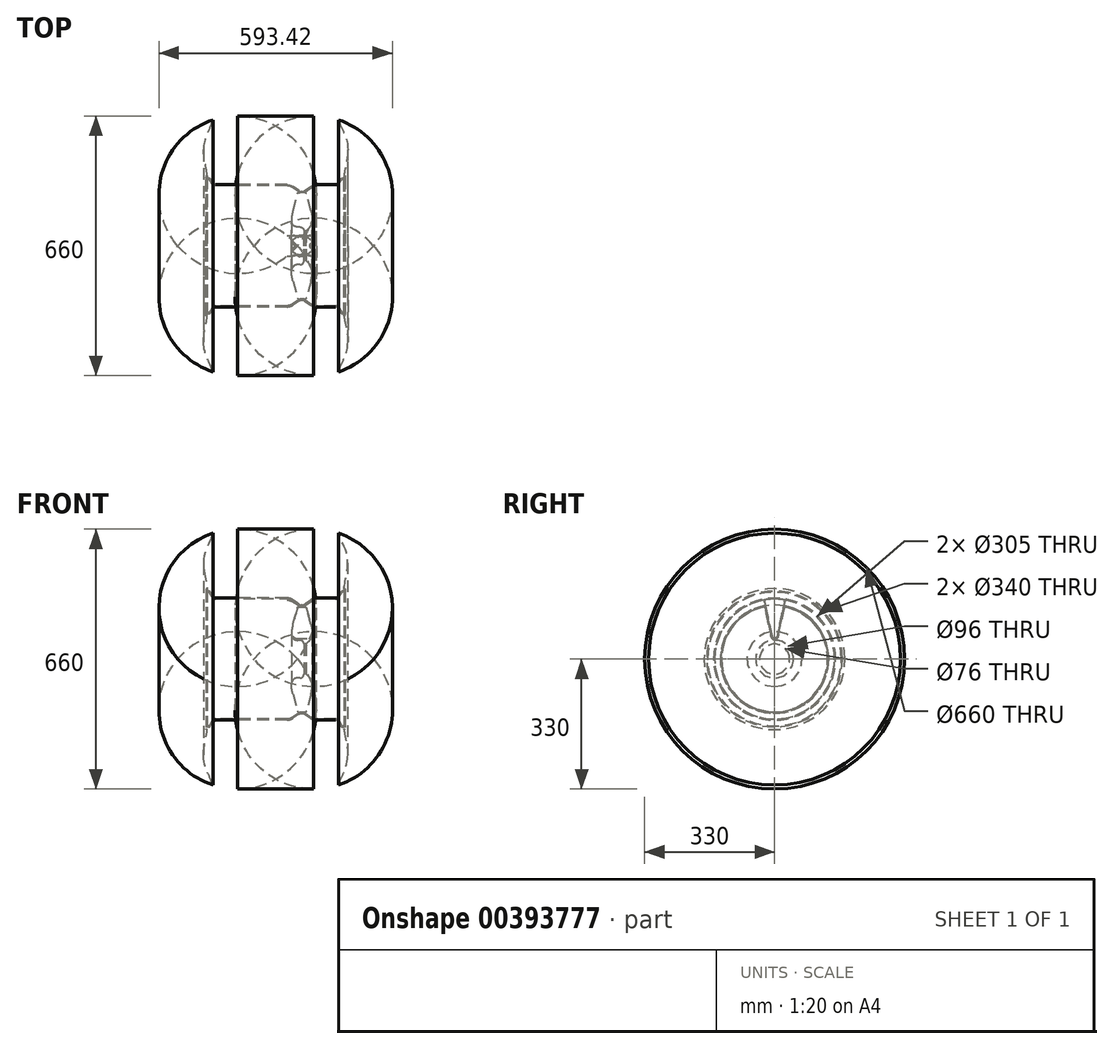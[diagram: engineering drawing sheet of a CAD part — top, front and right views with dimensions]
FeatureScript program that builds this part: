
annotation { "Feature Type Name" : "Feature", "Feature Type Description" : "" }
export const myFeature = defineFeature(function(context is Context, id is Id, definition is map)
    precondition{}
    {
        {
            var Q0;
            Q0=qCreatedBy(makeId("Front.planeOp"),FACE);
            var sketch = newSketch(context, id + "F0", { "sketchPlane" : qUnion([Q0])});
            skLineSegment(sketch, "E0", {"start": v(42.96, 147.98) * mm, "end": v(57.63, 137.71) * mm});
            skLineSegment(sketch, "E1", {"start": v(66.23, 135) * mm, "end": v(66.77, 135) * mm});
            skLineSegment(sketch, "E2", {"start": v(75.37, 137.71) * mm, "end": v(90.04, 147.98) * mm});
            skLineSegment(sketch, "E3", {"start": v(104.38, 152.5) * mm, "end": v(152.7, 152.5) * mm});
            skLineSegment(sketch, "E4", {"start": v(170.82, 170) * mm, "end": v(172.5, 170) * mm});
            skLineSegment(sketch, "E5", {"start": v(176.5, 174) * mm, "end": v(176.5, 178) * mm});
            skLineSegment(sketch, "E6", {"start": v(-170.82, 170) * mm, "end": v(-172.5, 170) * mm});
            skLineSegment(sketch, "E7", {"start": v(-176.5, 174) * mm, "end": v(-176.5, 178) * mm});
            skLineSegment(sketch, "E8", {"start": v(-152.7, 152.5) * mm, "end": v(28.62, 152.5) * mm});
            skLineSegment(sketch, "E9", {"start": v(-167.35, 167.98) * mm, "end": v(-161.38, 157.54) * mm});
            skLineSegment(sketch, "E10", {"start": v(161.38, 157.54) * mm, "end": v(167.35, 167.98) * mm});
            skPoint(sketch, "E11.visualSharp", {"position": v(176.5, 170) * mm});
            skArc(sketch, "E11.filletArc", {"start": v(172.5, 170) * mm, "mid": v(175.33, 171.17) * mm, "end": v(176.5, 174) * mm});
            skPoint(sketch, "E12.visualSharp", {"position": v(-176.5, 170) * mm});
            skArc(sketch, "E12.filletArc", {"start": v(-176.5, 174) * mm, "mid": v(-175.33, 171.17) * mm, "end": v(-172.5, 170) * mm});
            skPoint(sketch, "E13.visualSharp", {"position": v(-158.5, 152.5) * mm});
            skArc(sketch, "E13.filletArc", {"start": v(-161.38, 157.54) * mm, "mid": v(-157.72, 153.85) * mm, "end": v(-152.7, 152.5) * mm});
            skPoint(sketch, "E14.visualSharp", {"position": v(158.5, 152.5) * mm});
            skArc(sketch, "E14.filletArc", {"start": v(152.7, 152.5) * mm, "mid": v(157.72, 153.85) * mm, "end": v(161.38, 157.54) * mm});
            skPoint(sketch, "E15.visualSharp", {"position": v(-168.5, 170) * mm});
            skArc(sketch, "E15.filletArc", {"start": v(-167.35, 167.98) * mm, "mid": v(-168.81, 169.46) * mm, "end": v(-170.82, 170) * mm});
            skPoint(sketch, "E16.visualSharp", {"position": v(168.5, 170) * mm});
            skArc(sketch, "E16.filletArc", {"start": v(170.82, 170) * mm, "mid": v(168.81, 169.46) * mm, "end": v(167.35, 167.98) * mm});
            skPoint(sketch, "E17.visualSharp", {"position": v(36.5, 152.5) * mm});
            skArc(sketch, "E17.filletArc", {"start": v(42.96, 147.98) * mm, "mid": v(36.14, 151.34) * mm, "end": v(28.62, 152.5) * mm});
            skPoint(sketch, "E18.visualSharp", {"position": v(96.5, 152.5) * mm});
            skArc(sketch, "E18.filletArc", {"start": v(104.38, 152.5) * mm, "mid": v(96.86, 151.34) * mm, "end": v(90.04, 147.98) * mm});
            skPoint(sketch, "E19.visualSharp", {"position": v(71.5, 135) * mm});
            skArc(sketch, "E19.filletArc", {"start": v(66.77, 135) * mm, "mid": v(71.28, 135.7) * mm, "end": v(75.37, 137.71) * mm});
            skPoint(sketch, "E20.visualSharp", {"position": v(61.5, 135) * mm});
            skArc(sketch, "E20.filletArc", {"start": v(57.63, 137.71) * mm, "mid": v(61.72, 135.7) * mm, "end": v(66.23, 135) * mm});
            skLineSegment(sketch, "E21.0", {"start": v(174, 174) * mm, "end": v(174, 178) * mm});
            skArc(sketch, "E21.1", {"start": v(172.5, 172.5) * mm, "mid": v(173.56, 172.94) * mm, "end": v(174, 174) * mm});
            skLineSegment(sketch, "E21.2", {"start": v(170.82, 172.5) * mm, "end": v(172.5, 172.5) * mm});
            skArc(sketch, "E21.3", {"start": v(170.82, 172.5) * mm, "mid": v(167.56, 171.62) * mm, "end": v(165.18, 169.22) * mm});
            skLineSegment(sketch, "E21.4", {"start": v(159.2, 158.78) * mm, "end": v(165.18, 169.22) * mm});
            skArc(sketch, "E21.5", {"start": v(152.7, 155) * mm, "mid": v(156.46, 156.01) * mm, "end": v(159.2, 158.78) * mm});
            skLineSegment(sketch, "E21.6", {"start": v(104.38, 155) * mm, "end": v(152.7, 155) * mm});
            skArc(sketch, "E21.7", {"start": v(104.38, 155) * mm, "mid": v(96.11, 153.73) * mm, "end": v(88.61, 150.03) * mm});
            skLineSegment(sketch, "E21.8", {"start": v(73.94, 139.76) * mm, "end": v(88.61, 150.03) * mm});
            skArc(sketch, "E21.9", {"start": v(66.77, 137.5) * mm, "mid": v(70.53, 138.08) * mm, "end": v(73.94, 139.76) * mm});
            skLineSegment(sketch, "E21.10", {"start": v(66.23, 137.5) * mm, "end": v(66.77, 137.5) * mm});
            skArc(sketch, "E21.11", {"start": v(-165.18, 169.22) * mm, "mid": v(-167.56, 171.62) * mm, "end": v(-170.82, 172.5) * mm});
            skLineSegment(sketch, "E21.12", {"start": v(-170.82, 172.5) * mm, "end": v(-172.5, 172.5) * mm});
            skArc(sketch, "E21.13", {"start": v(-174, 174) * mm, "mid": v(-173.56, 172.94) * mm, "end": v(-172.5, 172.5) * mm});
            skLineSegment(sketch, "E21.14", {"start": v(-174, 174) * mm, "end": v(-174, 178) * mm});
            skLineSegment(sketch, "E21.15", {"start": v(-165.18, 169.22) * mm, "end": v(-159.2, 158.78) * mm});
            skArc(sketch, "E21.16", {"start": v(-159.2, 158.78) * mm, "mid": v(-156.46, 156.01) * mm, "end": v(-152.7, 155) * mm});
            skLineSegment(sketch, "E21.17", {"start": v(-152.7, 155) * mm, "end": v(28.62, 155) * mm});
            skArc(sketch, "E21.18", {"start": v(44.39, 150.03) * mm, "mid": v(36.89, 153.73) * mm, "end": v(28.62, 155) * mm});
            skLineSegment(sketch, "E21.19", {"start": v(44.39, 150.03) * mm, "end": v(59.06, 139.76) * mm});
            skArc(sketch, "E21.20", {"start": v(59.06, 139.76) * mm, "mid": v(62.47, 138.08) * mm, "end": v(66.23, 137.5) * mm});
            skLineSegment(sketch, "E22", {"start": v(175.5, 179) * mm, "end": v(175, 179) * mm});
            skLineSegment(sketch, "E23", {"start": v(-175.5, 179) * mm, "end": v(-175, 179) * mm});
            skPoint(sketch, "E24.visualSharp", {"position": v(-176.5, 179) * mm});
            skArc(sketch, "E24.filletArc", {"start": v(-175.5, 179) * mm, "mid": v(-176.2, 178.7) * mm, "end": v(-176.5, 178) * mm});
            skPoint(sketch, "E25.visualSharp", {"position": v(-174, 179) * mm});
            skArc(sketch, "E25.filletArc", {"start": v(-174, 178) * mm, "mid": v(-174.3, 178.7) * mm, "end": v(-175, 179) * mm});
            skPoint(sketch, "E26.visualSharp", {"position": v(174, 179) * mm});
            skArc(sketch, "E26.filletArc", {"start": v(175, 179) * mm, "mid": v(174.3, 178.7) * mm, "end": v(174, 178) * mm});
            skPoint(sketch, "E27.visualSharp", {"position": v(176.5, 179) * mm});
            skArc(sketch, "E27.filletArc", {"start": v(176.5, 178) * mm, "mid": v(176.2, 178.7) * mm, "end": v(175.5, 179) * mm});
            skLineSegment(sketch, "E28", {"start": v(-244.06, 0) * mm, "end": v(333.32, 0) * mm, "construction": true});
            skLineSegment(sketch, "E29", {"start": v(76.33, 138.38) * mm, "end": v(89.6, 88.88) * mm});
            skArc(sketch, "E30", {"start": v(89.6, 88.88) * mm, "mid": v(92.14, 76.05) * mm, "end": v(93, 63) * mm});
            skLineSegment(sketch, "E31", {"start": v(93, 63) * mm, "end": v(93, 94.03) * mm, "construction": true});
            skLineSegment(sketch, "E32", {"start": v(61.79, 48) * mm, "end": v(55.2, 48) * mm});
            skArc(sketch, "E33", {"start": v(55.2, 48) * mm, "mid": v(44.6, 52.4) * mm, "end": v(40.2, 63) * mm});
            skArc(sketch, "E34", {"start": v(40.2, 63) * mm, "mid": v(41.06, 76.05) * mm, "end": v(43.6, 88.88) * mm});
            skLineSegment(sketch, "E35", {"start": v(40.2, 63) * mm, "end": v(40.2, 94.03) * mm, "construction": true});
            skLineSegment(sketch, "E36", {"start": v(43.6, 88.88) * mm, "end": v(56.84, 138.26) * mm});
            skLineSegment(sketch, "E37", {"start": v(71.79, 38) * mm, "end": v(71.79, 38) * mm});
            skLineSegment(sketch, "E38", {"start": v(71.79, 38) * mm, "end": v(76.79, 38) * mm});
            skLineSegment(sketch, "E39", {"start": v(76.79, 38) * mm, "end": v(86.79, 48) * mm});
            skPoint(sketch, "E40.visualSharp", {"position": v(71.79, 48) * mm});
            skArc(sketch, "E40.filletArc", {"start": v(71.79, 38) * mm, "mid": v(68.86, 45.07) * mm, "end": v(61.79, 48) * mm});
            skArc(sketch, "E41", {"start": v(93, 63) * mm, "mid": v(91.39, 54.88) * mm, "end": v(86.79, 48) * mm});
            skFitSpline(sketch, "E42", {"points": [v(174, 178) * mm, v(174.59, 185.53) * mm, v(180.27, 215) * mm, v(181.17, 263.96) * mm, v(164.85, 306.38) * mm, v(162.5, 319.35) * mm], "startDerivative": vector(0, 85.85) * mm, "endDerivative": vector(0, 123.55) * mm});
            skLineSegment(sketch, "E43", {"start": v(162.5, 319.35) * mm, "end": v(162.5, 293.42) * mm, "construction": true});
            skFitSpline(sketch, "E44", {"points": [v(-162.5, 319.35) * mm, v(-164.85, 306.38) * mm, v(-181.17, 263.96) * mm, v(-180.27, 215) * mm, v(-174.59, 185.53) * mm, v(-174, 178) * mm], "startDerivative": vector(0, -123.55) * mm, "endDerivative": vector(0, -85.85) * mm});
            skLineSegment(sketch, "E45", {"start": v(-162.5, 319.35) * mm, "end": v(-162.5, 293.42) * mm, "construction": true});
            skArc(sketch, "E46.filletArc", {"start": v(162.6, 315.55) * mm, "mid": v(161.56, 318.3) * mm, "end": v(159.16, 320) * mm});
            skArc(sketch, "E47.filletArc", {"start": v(-159.16, 320) * mm, "mid": v(-161.56, 318.3) * mm, "end": v(-162.6, 315.55) * mm});
            skPoint(sketch, "E48", {"position": v(162.5, 306.38) * mm});
            skArc(sketch, "E49", {"start": v(-159.16, 320) * mm, "mid": v(-128.33, 327.48) * mm, "end": v(-96.71, 330) * mm});
            skArc(sketch, "E50", {"start": v(159.16, 320) * mm, "mid": v(128.33, 327.48) * mm, "end": v(96.71, 330) * mm});
            skLineSegment(sketch, "E51", {"start": v(-96.71, 330) * mm, "end": v(96.71, 330) * mm});
            skSolve(sketch);
        }
        {
            var Q0;
            Q0=qCreatedBy(makeId("Right.planeOp"),FACE);
            var sketch = newSketch(context, id + "F1", { "sketchPlane" : qUnion([Q0])});
            skArc(sketch, "E52", {"start": v(-29.75, 149.57) * mm, "mid": v(0, 152.5) * mm, "end": v(29.75, 149.57) * mm, "construction": true});
            skLineSegment(sketch, "E53", {"start": v(-29.75, 149.57) * mm, "end": v(0, 0) * mm, "construction": true});
            skLineSegment(sketch, "E54", {"start": v(29.75, 149.57) * mm, "end": v(0, 0) * mm, "construction": true});
            skArc(sketch, "E55", {"start": v(10.34, 51.98) * mm, "mid": v(0, 53) * mm, "end": v(-10.34, 51.98) * mm, "construction": true});
            skLineSegment(sketch, "E56", {"start": v(0, 0) * mm, "end": v(-34.81, 197.43) * mm, "construction": true});
            skLineSegment(sketch, "E57", {"start": v(0, 0) * mm, "end": v(34.81, 197.43) * mm, "construction": true});
            skArc(sketch, "E58", {"start": v(26.48, 150.18) * mm, "mid": v(0, 152.5) * mm, "end": v(-26.48, 150.18) * mm});
            skLineSegment(sketch, "E59", {"start": v(0, 0) * mm, "end": v(19.74, 187.83) * mm, "construction": true});
            skLineSegment(sketch, "E60", {"start": v(0, 0) * mm, "end": v(-19.74, 187.83) * mm, "construction": true});
            skLineSegment(sketch, "E61", {"start": v(-6.78, 58.48) * mm, "end": v(-26.48, 150.18) * mm});
            skLineSegment(sketch, "E62", {"start": v(6.78, 58.48) * mm, "end": v(26.48, 150.18) * mm});
            skPoint(sketch, "E63.visualSharp", {"position": v(-5.54, 52.7) * mm});
            skArc(sketch, "E63.filletArc", {"start": v(-6.78, 58.48) * mm, "mid": v(-4.36, 54.54) * mm, "end": v(0, 53) * mm});
            skPoint(sketch, "E64.visualSharp", {"position": v(5.54, 52.7) * mm});
            skArc(sketch, "E64.filletArc", {"start": v(0, 53) * mm, "mid": v(4.36, 54.54) * mm, "end": v(6.78, 58.48) * mm});
            skSolve(sketch);
        }
        {
            var Q0;
            Q0=makeQuery(id+"F0.imprint","IMPRINT",FACE,{"disambiguationData":[TD([[makeQuery(id+"F0.imprint","IMPRINT",EDGE,{"derivedFrom":sQuery(id+"F0.wireOp",EDGE,"E3")}),1.0]])]});
            var Q1;
            Q1=sQuery(id+"F0.wireOp",EDGE,"E28");
            revolve(context, id + "F2", {"entities" : qUnion([Q0]), "axis" : qUnion([Q1]), "revolveType" : RevolveType.FULL});
        }
        {
            var Q0;
            Q0=makeQuery(id+"F0.imprint","IMPRINT",FACE,{"disambiguationData":[TD([[makeQuery(id+"F0.imprint","IMPRINT",EDGE,{"derivedFrom":sQuery(id+"F0.wireOp",EDGE,"E1")}),-1.0]])]});
            var Q1;
            Q1=sQuery(id+"F0.wireOp",EDGE,"E28");
            revolve(context, id + "F3", {"entities" : qUnion([Q0]), "axis" : qUnion([Q1]), "revolveType" : RevolveType.FULL});
        }
        {
            var Q0;
            Q0=makeQuery(id+"F1.imprint","IMPRINT",FACE,{"disambiguationData":[TD([[makeQuery(id+"F1.imprint","IMPRINT",EDGE,{"derivedFrom":sQuery(id+"F1.wireOp",EDGE,"E58")}),1.0]])]});
            extrude(context, id + "F4", {"entities" : qUnion([Q0]), "operationType" : NewBodyOperationType.REMOVE, "endBound" : BoundingType.THROUGH_ALL, "oppositeDirection" : true, "depth" : 25 * mm, "hasSecondDirection" : true, "secondDirectionBound" : SecondDirectionBoundingType.THROUGH_ALL, "secondDirectionOppositeDirection" : false, "secondDirectionDepth" : 25 * mm});
        }
        {
            var Q0;
            Q0=makeQuery(id+"F4.boolean.opBoolean","INTERSECT",EDGE,{"derivedFrom":[makeQuery(id+"F3.opRevolve","SWEPT_FACE",FACE,{"disambiguationData":[OSD([sQuery(id+"F0.wireOp",EDGE,"E34")])]}),makeQuery(id+"F4.opExtrude","SWEPT_FACE",FACE,{"disambiguationData":[OSD([sQuery(id+"F1.wireOp",EDGE,"E62")])]})]});
            var Q1;
            Q1=makeQuery(id+"F1MoAnU7Y2teXVl_2.1.F4.boolean.opBoolean","INTERSECT",EDGE,{"derivedFrom":[makeQuery(id+"F3.opRevolve","SWEPT_FACE",FACE,{"disambiguationData":[OSD([sQuery(id+"F0.wireOp",EDGE,"E34")])]}),makeQuery(id+"F1MoAnU7Y2teXVl_2.1.F4.opExtrude","SWEPT_FACE",FACE,{"disambiguationData":[OSD([sQuery(id+"F1.wireOp",EDGE,"E62")])]})]});
            var Q2;
            {var subQ0=sQuery(id+"F1.wireOp",EDGE,"E62");Q2=makeQuery(id+"F1MoAnU7Y2teXVl_2.2.F4.boolean.opBoolean","INTERSECT",EDGE,{"derivedFrom":[makeQuery(id+"F1MoAnU7Y2teXVl_2.1.F4.boolean.opBoolean","SPLIT",FACE,{"disambiguationData":[TD([makeQuery(id+"F4.boolean.opBoolean","COPY",FACE,{"derivedFrom":makeQuery(id+"F4.opExtrude","SWEPT_FACE",FACE,{"disambiguationData":[OSD([subQ0])]})})])],"derivedFrom":makeQuery(id+"F3.opRevolve","SWEPT_FACE",FACE,{"disambiguationData":[OSD([sQuery(id+"F0.wireOp",EDGE,"E34")])]})}),makeQuery(id+"F1MoAnU7Y2teXVl_2.2.F4.opExtrude","SWEPT_FACE",FACE,{"disambiguationData":[OSD([subQ0])]})]});}
            var Q3;
            {var subQ0=sQuery(id+"F1.wireOp",EDGE,"E62");var subQ3=makeQuery(id+"F4.boolean.opBoolean","COPY",FACE,{"derivedFrom":makeQuery(id+"F4.opExtrude","SWEPT_FACE",FACE,{"disambiguationData":[OSD([subQ0])]})});Q3=makeQuery(id+"F1MoAnU7Y2teXVl_2.3.F4.boolean.opBoolean","INTERSECT",EDGE,{"derivedFrom":[makeQuery(id+"F1MoAnU7Y2teXVl_2.2.F4.boolean.opBoolean","SPLIT",FACE,{"disambiguationData":[TD([subQ3])],"derivedFrom":makeQuery(id+"F1MoAnU7Y2teXVl_2.1.F4.boolean.opBoolean","SPLIT",FACE,{"disambiguationData":[TD([subQ3])],"derivedFrom":makeQuery(id+"F3.opRevolve","SWEPT_FACE",FACE,{"disambiguationData":[OSD([sQuery(id+"F0.wireOp",EDGE,"E34")])]})})}),makeQuery(id+"F1MoAnU7Y2teXVl_2.3.F4.opExtrude","SWEPT_FACE",FACE,{"disambiguationData":[OSD([subQ0])]})]});}
            var Q4;
            {var subQ0=sQuery(id+"F1.wireOp",EDGE,"E62");var subQ3=makeQuery(id+"F4.boolean.opBoolean","COPY",FACE,{"derivedFrom":makeQuery(id+"F4.opExtrude","SWEPT_FACE",FACE,{"disambiguationData":[OSD([subQ0])]})});Q4=makeQuery(id+"F1MoAnU7Y2teXVl_2.4.F4.boolean.opBoolean","INTERSECT",EDGE,{"derivedFrom":[makeQuery(id+"F1MoAnU7Y2teXVl_2.3.F4.boolean.opBoolean","SPLIT",FACE,{"disambiguationData":[TD([subQ3])],"derivedFrom":makeQuery(id+"F1MoAnU7Y2teXVl_2.2.F4.boolean.opBoolean","SPLIT",FACE,{"disambiguationData":[TD([subQ3])],"derivedFrom":makeQuery(id+"F1MoAnU7Y2teXVl_2.1.F4.boolean.opBoolean","SPLIT",FACE,{"disambiguationData":[TD([subQ3])],"derivedFrom":makeQuery(id+"F3.opRevolve","SWEPT_FACE",FACE,{"disambiguationData":[OSD([sQuery(id+"F0.wireOp",EDGE,"E34")])]})})})}),makeQuery(id+"F1MoAnU7Y2teXVl_2.4.F4.opExtrude","SWEPT_FACE",FACE,{"disambiguationData":[OSD([subQ0])]})]});}
            var Q5;
            {var subQ0=sQuery(id+"F1.wireOp",EDGE,"E62");var subQ3=makeQuery(id+"F4.boolean.opBoolean","COPY",FACE,{"derivedFrom":makeQuery(id+"F4.opExtrude","SWEPT_FACE",FACE,{"disambiguationData":[OSD([subQ0])]})});Q5=makeQuery(id+"F1MoAnU7Y2teXVl_2.5.F4.boolean.opBoolean","INTERSECT",EDGE,{"derivedFrom":[makeQuery(id+"F1MoAnU7Y2teXVl_2.4.F4.boolean.opBoolean","SPLIT",FACE,{"disambiguationData":[TD([subQ3])],"derivedFrom":makeQuery(id+"F1MoAnU7Y2teXVl_2.3.F4.boolean.opBoolean","SPLIT",FACE,{"disambiguationData":[TD([subQ3])],"derivedFrom":makeQuery(id+"F1MoAnU7Y2teXVl_2.2.F4.boolean.opBoolean","SPLIT",FACE,{"disambiguationData":[TD([subQ3])],"derivedFrom":makeQuery(id+"F1MoAnU7Y2teXVl_2.1.F4.boolean.opBoolean","SPLIT",FACE,{"disambiguationData":[TD([subQ3])],"derivedFrom":makeQuery(id+"F3.opRevolve","SWEPT_FACE",FACE,{"disambiguationData":[OSD([sQuery(id+"F0.wireOp",EDGE,"E34")])]})})})})}),makeQuery(id+"F1MoAnU7Y2teXVl_2.5.F4.opExtrude","SWEPT_FACE",FACE,{"disambiguationData":[OSD([subQ0])]})]});}
            var Q6;
            {var subQ0=sQuery(id+"F1.wireOp",EDGE,"E62");var subQ4=makeQuery(id+"F4.boolean.opBoolean","COPY",FACE,{"derivedFrom":makeQuery(id+"F4.opExtrude","SWEPT_FACE",FACE,{"disambiguationData":[OSD([subQ0])]})});Q6=makeQuery(id+"F1MoAnU7Y2teXVl_2.6.F4.boolean.opBoolean","INTERSECT",EDGE,{"derivedFrom":[makeQuery(id+"F1MoAnU7Y2teXVl_2.5.F4.boolean.opBoolean","SPLIT",FACE,{"disambiguationData":[TD([subQ4])],"derivedFrom":makeQuery(id+"F1MoAnU7Y2teXVl_2.4.F4.boolean.opBoolean","SPLIT",FACE,{"disambiguationData":[TD([subQ4])],"derivedFrom":makeQuery(id+"F1MoAnU7Y2teXVl_2.3.F4.boolean.opBoolean","SPLIT",FACE,{"disambiguationData":[TD([subQ4])],"derivedFrom":makeQuery(id+"F1MoAnU7Y2teXVl_2.2.F4.boolean.opBoolean","SPLIT",FACE,{"disambiguationData":[TD([subQ4])],"derivedFrom":makeQuery(id+"F1MoAnU7Y2teXVl_2.1.F4.boolean.opBoolean","SPLIT",FACE,{"disambiguationData":[TD([subQ4])],"derivedFrom":makeQuery(id+"F3.opRevolve","SWEPT_FACE",FACE,{"disambiguationData":[OSD([sQuery(id+"F0.wireOp",EDGE,"E34")])]})})})})})}),makeQuery(id+"F1MoAnU7Y2teXVl_2.6.F4.opExtrude","SWEPT_FACE",FACE,{"disambiguationData":[OSD([subQ0])]})]});}
            var Q7;
            {var subQ0=sQuery(id+"F1.wireOp",EDGE,"E62");var subQ3=makeQuery(id+"F4.boolean.opBoolean","COPY",FACE,{"derivedFrom":makeQuery(id+"F4.opExtrude","SWEPT_FACE",FACE,{"disambiguationData":[OSD([subQ0])]})});Q7=makeQuery(id+"F1MoAnU7Y2teXVl_2.7.F4.boolean.opBoolean","INTERSECT",EDGE,{"derivedFrom":[makeQuery(id+"F1MoAnU7Y2teXVl_2.6.F4.boolean.opBoolean","SPLIT",FACE,{"disambiguationData":[TD([subQ3])],"derivedFrom":makeQuery(id+"F1MoAnU7Y2teXVl_2.5.F4.boolean.opBoolean","SPLIT",FACE,{"disambiguationData":[TD([subQ3])],"derivedFrom":makeQuery(id+"F1MoAnU7Y2teXVl_2.4.F4.boolean.opBoolean","SPLIT",FACE,{"disambiguationData":[TD([subQ3])],"derivedFrom":makeQuery(id+"F1MoAnU7Y2teXVl_2.3.F4.boolean.opBoolean","SPLIT",FACE,{"disambiguationData":[TD([subQ3])],"derivedFrom":makeQuery(id+"F1MoAnU7Y2teXVl_2.2.F4.boolean.opBoolean","SPLIT",FACE,{"disambiguationData":[TD([subQ3])],"derivedFrom":makeQuery(id+"F1MoAnU7Y2teXVl_2.1.F4.boolean.opBoolean","SPLIT",FACE,{"disambiguationData":[TD([subQ3])],"derivedFrom":makeQuery(id+"F3.opRevolve","SWEPT_FACE",FACE,{"disambiguationData":[OSD([sQuery(id+"F0.wireOp",EDGE,"E34")])]})})})})})})}),makeQuery(id+"F1MoAnU7Y2teXVl_2.7.F4.opExtrude","SWEPT_FACE",FACE,{"disambiguationData":[OSD([subQ0])]})]});}
            var Q8;
            {var subQ0=sQuery(id+"F1.wireOp",EDGE,"E62");var subQ3=makeQuery(id+"F4.boolean.opBoolean","COPY",FACE,{"derivedFrom":makeQuery(id+"F4.opExtrude","SWEPT_FACE",FACE,{"disambiguationData":[OSD([subQ0])]})});Q8=makeQuery(id+"F1MoAnU7Y2teXVl_2.8.F4.boolean.opBoolean","INTERSECT",EDGE,{"derivedFrom":[makeQuery(id+"F1MoAnU7Y2teXVl_2.7.F4.boolean.opBoolean","SPLIT",FACE,{"disambiguationData":[TD([subQ3])],"derivedFrom":makeQuery(id+"F1MoAnU7Y2teXVl_2.6.F4.boolean.opBoolean","SPLIT",FACE,{"disambiguationData":[TD([subQ3])],"derivedFrom":makeQuery(id+"F1MoAnU7Y2teXVl_2.5.F4.boolean.opBoolean","SPLIT",FACE,{"disambiguationData":[TD([subQ3])],"derivedFrom":makeQuery(id+"F1MoAnU7Y2teXVl_2.4.F4.boolean.opBoolean","SPLIT",FACE,{"disambiguationData":[TD([subQ3])],"derivedFrom":makeQuery(id+"F1MoAnU7Y2teXVl_2.3.F4.boolean.opBoolean","SPLIT",FACE,{"disambiguationData":[TD([subQ3])],"derivedFrom":makeQuery(id+"F1MoAnU7Y2teXVl_2.2.F4.boolean.opBoolean","SPLIT",FACE,{"disambiguationData":[TD([subQ3])],"derivedFrom":makeQuery(id+"F1MoAnU7Y2teXVl_2.1.F4.boolean.opBoolean","SPLIT",FACE,{"disambiguationData":[TD([subQ3])],"derivedFrom":makeQuery(id+"F3.opRevolve","SWEPT_FACE",FACE,{"disambiguationData":[OSD([sQuery(id+"F0.wireOp",EDGE,"E34")])]})})})})})})})}),makeQuery(id+"F1MoAnU7Y2teXVl_2.8.F4.opExtrude","SWEPT_FACE",FACE,{"disambiguationData":[OSD([subQ0])]})]});}
            var Q9;
            {var subQ0=sQuery(id+"F1.wireOp",EDGE,"E62");var subQ3=makeQuery(id+"F4.boolean.opBoolean","COPY",FACE,{"derivedFrom":makeQuery(id+"F4.opExtrude","SWEPT_FACE",FACE,{"disambiguationData":[OSD([subQ0])]})});Q9=makeQuery(id+"F1MoAnU7Y2teXVl_2.9.F4.boolean.opBoolean","INTERSECT",EDGE,{"derivedFrom":[makeQuery(id+"F1MoAnU7Y2teXVl_2.8.F4.boolean.opBoolean","SPLIT",FACE,{"disambiguationData":[TD([subQ3])],"derivedFrom":makeQuery(id+"F1MoAnU7Y2teXVl_2.7.F4.boolean.opBoolean","SPLIT",FACE,{"disambiguationData":[TD([subQ3])],"derivedFrom":makeQuery(id+"F1MoAnU7Y2teXVl_2.6.F4.boolean.opBoolean","SPLIT",FACE,{"disambiguationData":[TD([subQ3])],"derivedFrom":makeQuery(id+"F1MoAnU7Y2teXVl_2.5.F4.boolean.opBoolean","SPLIT",FACE,{"disambiguationData":[TD([subQ3])],"derivedFrom":makeQuery(id+"F1MoAnU7Y2teXVl_2.4.F4.boolean.opBoolean","SPLIT",FACE,{"disambiguationData":[TD([subQ3])],"derivedFrom":makeQuery(id+"F1MoAnU7Y2teXVl_2.3.F4.boolean.opBoolean","SPLIT",FACE,{"disambiguationData":[TD([subQ3])],"derivedFrom":makeQuery(id+"F1MoAnU7Y2teXVl_2.2.F4.boolean.opBoolean","SPLIT",FACE,{"disambiguationData":[TD([subQ3])],"derivedFrom":makeQuery(id+"F1MoAnU7Y2teXVl_2.1.F4.boolean.opBoolean","SPLIT",FACE,{"disambiguationData":[TD([subQ3])],"derivedFrom":makeQuery(id+"F3.opRevolve","SWEPT_FACE",FACE,{"disambiguationData":[OSD([sQuery(id+"F0.wireOp",EDGE,"E34")])]})})})})})})})})}),makeQuery(id+"F1MoAnU7Y2teXVl_2.9.F4.opExtrude","SWEPT_FACE",FACE,{"disambiguationData":[OSD([subQ0])]})]});}
            var Q10;
            {var subQ0=sQuery(id+"F1.wireOp",EDGE,"E62");var subQ4=makeQuery(id+"F4.boolean.opBoolean","COPY",FACE,{"derivedFrom":makeQuery(id+"F4.opExtrude","SWEPT_FACE",FACE,{"disambiguationData":[OSD([subQ0])]})});Q10=makeQuery(id+"F1MoAnU7Y2teXVl_2.10.F4.boolean.opBoolean","INTERSECT",EDGE,{"derivedFrom":[makeQuery(id+"F1MoAnU7Y2teXVl_2.9.F4.boolean.opBoolean","SPLIT",FACE,{"disambiguationData":[TD([subQ4])],"derivedFrom":makeQuery(id+"F1MoAnU7Y2teXVl_2.8.F4.boolean.opBoolean","SPLIT",FACE,{"disambiguationData":[TD([subQ4])],"derivedFrom":makeQuery(id+"F1MoAnU7Y2teXVl_2.7.F4.boolean.opBoolean","SPLIT",FACE,{"disambiguationData":[TD([subQ4])],"derivedFrom":makeQuery(id+"F1MoAnU7Y2teXVl_2.6.F4.boolean.opBoolean","SPLIT",FACE,{"disambiguationData":[TD([subQ4])],"derivedFrom":makeQuery(id+"F1MoAnU7Y2teXVl_2.5.F4.boolean.opBoolean","SPLIT",FACE,{"disambiguationData":[TD([subQ4])],"derivedFrom":makeQuery(id+"F1MoAnU7Y2teXVl_2.4.F4.boolean.opBoolean","SPLIT",FACE,{"disambiguationData":[TD([subQ4])],"derivedFrom":makeQuery(id+"F1MoAnU7Y2teXVl_2.3.F4.boolean.opBoolean","SPLIT",FACE,{"disambiguationData":[TD([subQ4])],"derivedFrom":makeQuery(id+"F1MoAnU7Y2teXVl_2.2.F4.boolean.opBoolean","SPLIT",FACE,{"disambiguationData":[TD([subQ4])],"derivedFrom":makeQuery(id+"F1MoAnU7Y2teXVl_2.1.F4.boolean.opBoolean","SPLIT",FACE,{"disambiguationData":[TD([subQ4])],"derivedFrom":makeQuery(id+"F3.opRevolve","SWEPT_FACE",FACE,{"disambiguationData":[OSD([sQuery(id+"F0.wireOp",EDGE,"E34")])]})})})})})})})})})}),makeQuery(id+"F1MoAnU7Y2teXVl_2.10.F4.opExtrude","SWEPT_FACE",FACE,{"disambiguationData":[OSD([subQ0])]})]});}
            var Q11;
            {var subQ0=sQuery(id+"F1.wireOp",EDGE,"E62");var subQ3=makeQuery(id+"F4.boolean.opBoolean","COPY",FACE,{"derivedFrom":makeQuery(id+"F4.opExtrude","SWEPT_FACE",FACE,{"disambiguationData":[OSD([subQ0])]})});Q11=makeQuery(id+"F1MoAnU7Y2teXVl_2.11.F4.boolean.opBoolean","INTERSECT",EDGE,{"derivedFrom":[makeQuery(id+"F1MoAnU7Y2teXVl_2.10.F4.boolean.opBoolean","SPLIT",FACE,{"disambiguationData":[TD([subQ3])],"derivedFrom":makeQuery(id+"F1MoAnU7Y2teXVl_2.9.F4.boolean.opBoolean","SPLIT",FACE,{"disambiguationData":[TD([subQ3])],"derivedFrom":makeQuery(id+"F1MoAnU7Y2teXVl_2.8.F4.boolean.opBoolean","SPLIT",FACE,{"disambiguationData":[TD([subQ3])],"derivedFrom":makeQuery(id+"F1MoAnU7Y2teXVl_2.7.F4.boolean.opBoolean","SPLIT",FACE,{"disambiguationData":[TD([subQ3])],"derivedFrom":makeQuery(id+"F1MoAnU7Y2teXVl_2.6.F4.boolean.opBoolean","SPLIT",FACE,{"disambiguationData":[TD([subQ3])],"derivedFrom":makeQuery(id+"F1MoAnU7Y2teXVl_2.5.F4.boolean.opBoolean","SPLIT",FACE,{"disambiguationData":[TD([subQ3])],"derivedFrom":makeQuery(id+"F1MoAnU7Y2teXVl_2.4.F4.boolean.opBoolean","SPLIT",FACE,{"disambiguationData":[TD([subQ3])],"derivedFrom":makeQuery(id+"F1MoAnU7Y2teXVl_2.3.F4.boolean.opBoolean","SPLIT",FACE,{"disambiguationData":[TD([subQ3])],"derivedFrom":makeQuery(id+"F1MoAnU7Y2teXVl_2.2.F4.boolean.opBoolean","SPLIT",FACE,{"disambiguationData":[TD([subQ3])],"derivedFrom":makeQuery(id+"F1MoAnU7Y2teXVl_2.1.F4.boolean.opBoolean","SPLIT",FACE,{"disambiguationData":[TD([subQ3])],"derivedFrom":makeQuery(id+"F3.opRevolve","SWEPT_FACE",FACE,{"disambiguationData":[OSD([sQuery(id+"F0.wireOp",EDGE,"E34")])]})})})})})})})})})})}),makeQuery(id+"F1MoAnU7Y2teXVl_2.11.F4.opExtrude","SWEPT_FACE",FACE,{"disambiguationData":[OSD([subQ0])]})]});}
            var Q12;
            {var subQ0=sQuery(id+"F1.wireOp",EDGE,"E62");var subQ3=makeQuery(id+"F4.boolean.opBoolean","COPY",FACE,{"derivedFrom":makeQuery(id+"F4.opExtrude","SWEPT_FACE",FACE,{"disambiguationData":[OSD([subQ0])]})});Q12=makeQuery(id+"F1MoAnU7Y2teXVl_2.12.F4.boolean.opBoolean","INTERSECT",EDGE,{"derivedFrom":[makeQuery(id+"F1MoAnU7Y2teXVl_2.11.F4.boolean.opBoolean","SPLIT",FACE,{"disambiguationData":[TD([subQ3])],"derivedFrom":makeQuery(id+"F1MoAnU7Y2teXVl_2.10.F4.boolean.opBoolean","SPLIT",FACE,{"disambiguationData":[TD([subQ3])],"derivedFrom":makeQuery(id+"F1MoAnU7Y2teXVl_2.9.F4.boolean.opBoolean","SPLIT",FACE,{"disambiguationData":[TD([subQ3])],"derivedFrom":makeQuery(id+"F1MoAnU7Y2teXVl_2.8.F4.boolean.opBoolean","SPLIT",FACE,{"disambiguationData":[TD([subQ3])],"derivedFrom":makeQuery(id+"F1MoAnU7Y2teXVl_2.7.F4.boolean.opBoolean","SPLIT",FACE,{"disambiguationData":[TD([subQ3])],"derivedFrom":makeQuery(id+"F1MoAnU7Y2teXVl_2.6.F4.boolean.opBoolean","SPLIT",FACE,{"disambiguationData":[TD([subQ3])],"derivedFrom":makeQuery(id+"F1MoAnU7Y2teXVl_2.5.F4.boolean.opBoolean","SPLIT",FACE,{"disambiguationData":[TD([subQ3])],"derivedFrom":makeQuery(id+"F1MoAnU7Y2teXVl_2.4.F4.boolean.opBoolean","SPLIT",FACE,{"disambiguationData":[TD([subQ3])],"derivedFrom":makeQuery(id+"F1MoAnU7Y2teXVl_2.3.F4.boolean.opBoolean","SPLIT",FACE,{"disambiguationData":[TD([subQ3])],"derivedFrom":makeQuery(id+"F1MoAnU7Y2teXVl_2.2.F4.boolean.opBoolean","SPLIT",FACE,{"disambiguationData":[TD([subQ3])],"derivedFrom":makeQuery(id+"F1MoAnU7Y2teXVl_2.1.F4.boolean.opBoolean","SPLIT",FACE,{"disambiguationData":[TD([subQ3])],"derivedFrom":makeQuery(id+"F3.opRevolve","SWEPT_FACE",FACE,{"disambiguationData":[OSD([sQuery(id+"F0.wireOp",EDGE,"E34")])]})})})})})})})})})})})}),makeQuery(id+"F1MoAnU7Y2teXVl_2.12.F4.opExtrude","SWEPT_FACE",FACE,{"disambiguationData":[OSD([subQ0])]})]});}
            var Q13;
            {var subQ0=sQuery(id+"F1.wireOp",EDGE,"E62");var subQ3=makeQuery(id+"F4.boolean.opBoolean","COPY",FACE,{"derivedFrom":makeQuery(id+"F4.opExtrude","SWEPT_FACE",FACE,{"disambiguationData":[OSD([subQ0])]})});Q13=makeQuery(id+"F1MoAnU7Y2teXVl_2.13.F4.boolean.opBoolean","INTERSECT",EDGE,{"derivedFrom":[makeQuery(id+"F1MoAnU7Y2teXVl_2.12.F4.boolean.opBoolean","SPLIT",FACE,{"disambiguationData":[TD([subQ3])],"derivedFrom":makeQuery(id+"F1MoAnU7Y2teXVl_2.11.F4.boolean.opBoolean","SPLIT",FACE,{"disambiguationData":[TD([subQ3])],"derivedFrom":makeQuery(id+"F1MoAnU7Y2teXVl_2.10.F4.boolean.opBoolean","SPLIT",FACE,{"disambiguationData":[TD([subQ3])],"derivedFrom":makeQuery(id+"F1MoAnU7Y2teXVl_2.9.F4.boolean.opBoolean","SPLIT",FACE,{"disambiguationData":[TD([subQ3])],"derivedFrom":makeQuery(id+"F1MoAnU7Y2teXVl_2.8.F4.boolean.opBoolean","SPLIT",FACE,{"disambiguationData":[TD([subQ3])],"derivedFrom":makeQuery(id+"F1MoAnU7Y2teXVl_2.7.F4.boolean.opBoolean","SPLIT",FACE,{"disambiguationData":[TD([subQ3])],"derivedFrom":makeQuery(id+"F1MoAnU7Y2teXVl_2.6.F4.boolean.opBoolean","SPLIT",FACE,{"disambiguationData":[TD([subQ3])],"derivedFrom":makeQuery(id+"F1MoAnU7Y2teXVl_2.5.F4.boolean.opBoolean","SPLIT",FACE,{"disambiguationData":[TD([subQ3])],"derivedFrom":makeQuery(id+"F1MoAnU7Y2teXVl_2.4.F4.boolean.opBoolean","SPLIT",FACE,{"disambiguationData":[TD([subQ3])],"derivedFrom":makeQuery(id+"F1MoAnU7Y2teXVl_2.3.F4.boolean.opBoolean","SPLIT",FACE,{"disambiguationData":[TD([subQ3])],"derivedFrom":makeQuery(id+"F1MoAnU7Y2teXVl_2.2.F4.boolean.opBoolean","SPLIT",FACE,{"disambiguationData":[TD([subQ3])],"derivedFrom":makeQuery(id+"F1MoAnU7Y2teXVl_2.1.F4.boolean.opBoolean","SPLIT",FACE,{"disambiguationData":[TD([subQ3])],"derivedFrom":makeQuery(id+"F3.opRevolve","SWEPT_FACE",FACE,{"disambiguationData":[OSD([sQuery(id+"F0.wireOp",EDGE,"E34")])]})})})})})})})})})})})})}),makeQuery(id+"F1MoAnU7Y2teXVl_2.13.F4.opExtrude","SWEPT_FACE",FACE,{"disambiguationData":[OSD([subQ0])]})]});}
            var Q14;
            {var subQ0=sQuery(id+"F1.wireOp",EDGE,"E62");var subQ4=makeQuery(id+"F4.boolean.opBoolean","COPY",FACE,{"derivedFrom":makeQuery(id+"F4.opExtrude","SWEPT_FACE",FACE,{"disambiguationData":[OSD([subQ0])]})});Q14=makeQuery(id+"F1MoAnU7Y2teXVl_2.14.F4.boolean.opBoolean","INTERSECT",EDGE,{"derivedFrom":[makeQuery(id+"F1MoAnU7Y2teXVl_2.13.F4.boolean.opBoolean","SPLIT",FACE,{"disambiguationData":[TD([subQ4])],"derivedFrom":makeQuery(id+"F1MoAnU7Y2teXVl_2.12.F4.boolean.opBoolean","SPLIT",FACE,{"disambiguationData":[TD([subQ4])],"derivedFrom":makeQuery(id+"F1MoAnU7Y2teXVl_2.11.F4.boolean.opBoolean","SPLIT",FACE,{"disambiguationData":[TD([subQ4])],"derivedFrom":makeQuery(id+"F1MoAnU7Y2teXVl_2.10.F4.boolean.opBoolean","SPLIT",FACE,{"disambiguationData":[TD([subQ4])],"derivedFrom":makeQuery(id+"F1MoAnU7Y2teXVl_2.9.F4.boolean.opBoolean","SPLIT",FACE,{"disambiguationData":[TD([subQ4])],"derivedFrom":makeQuery(id+"F1MoAnU7Y2teXVl_2.8.F4.boolean.opBoolean","SPLIT",FACE,{"disambiguationData":[TD([subQ4])],"derivedFrom":makeQuery(id+"F1MoAnU7Y2teXVl_2.7.F4.boolean.opBoolean","SPLIT",FACE,{"disambiguationData":[TD([subQ4])],"derivedFrom":makeQuery(id+"F1MoAnU7Y2teXVl_2.6.F4.boolean.opBoolean","SPLIT",FACE,{"disambiguationData":[TD([subQ4])],"derivedFrom":makeQuery(id+"F1MoAnU7Y2teXVl_2.5.F4.boolean.opBoolean","SPLIT",FACE,{"disambiguationData":[TD([subQ4])],"derivedFrom":makeQuery(id+"F1MoAnU7Y2teXVl_2.4.F4.boolean.opBoolean","SPLIT",FACE,{"disambiguationData":[TD([subQ4])],"derivedFrom":makeQuery(id+"F1MoAnU7Y2teXVl_2.3.F4.boolean.opBoolean","SPLIT",FACE,{"disambiguationData":[TD([subQ4])],"derivedFrom":makeQuery(id+"F1MoAnU7Y2teXVl_2.2.F4.boolean.opBoolean","SPLIT",FACE,{"disambiguationData":[TD([subQ4])],"derivedFrom":makeQuery(id+"F1MoAnU7Y2teXVl_2.1.F4.boolean.opBoolean","SPLIT",FACE,{"disambiguationData":[TD([subQ4])],"derivedFrom":makeQuery(id+"F3.opRevolve","SWEPT_FACE",FACE,{"disambiguationData":[OSD([sQuery(id+"F0.wireOp",EDGE,"E34")])]})})})})})})})})})})})})})}),makeQuery(id+"F1MoAnU7Y2teXVl_2.14.F4.opExtrude","SWEPT_FACE",FACE,{"disambiguationData":[OSD([subQ0])]})]});}
            var Q15;
            {var subQ0=sQuery(id+"F1.wireOp",EDGE,"E62");var subQ3=makeQuery(id+"F4.boolean.opBoolean","COPY",FACE,{"derivedFrom":makeQuery(id+"F4.opExtrude","SWEPT_FACE",FACE,{"disambiguationData":[OSD([subQ0])]})});Q15=makeQuery(id+"F1MoAnU7Y2teXVl_2.15.F4.boolean.opBoolean","INTERSECT",EDGE,{"derivedFrom":[makeQuery(id+"F1MoAnU7Y2teXVl_2.14.F4.boolean.opBoolean","SPLIT",FACE,{"disambiguationData":[TD([subQ3])],"derivedFrom":makeQuery(id+"F1MoAnU7Y2teXVl_2.13.F4.boolean.opBoolean","SPLIT",FACE,{"disambiguationData":[TD([subQ3])],"derivedFrom":makeQuery(id+"F1MoAnU7Y2teXVl_2.12.F4.boolean.opBoolean","SPLIT",FACE,{"disambiguationData":[TD([subQ3])],"derivedFrom":makeQuery(id+"F1MoAnU7Y2teXVl_2.11.F4.boolean.opBoolean","SPLIT",FACE,{"disambiguationData":[TD([subQ3])],"derivedFrom":makeQuery(id+"F1MoAnU7Y2teXVl_2.10.F4.boolean.opBoolean","SPLIT",FACE,{"disambiguationData":[TD([subQ3])],"derivedFrom":makeQuery(id+"F1MoAnU7Y2teXVl_2.9.F4.boolean.opBoolean","SPLIT",FACE,{"disambiguationData":[TD([subQ3])],"derivedFrom":makeQuery(id+"F1MoAnU7Y2teXVl_2.8.F4.boolean.opBoolean","SPLIT",FACE,{"disambiguationData":[TD([subQ3])],"derivedFrom":makeQuery(id+"F1MoAnU7Y2teXVl_2.7.F4.boolean.opBoolean","SPLIT",FACE,{"disambiguationData":[TD([subQ3])],"derivedFrom":makeQuery(id+"F1MoAnU7Y2teXVl_2.6.F4.boolean.opBoolean","SPLIT",FACE,{"disambiguationData":[TD([subQ3])],"derivedFrom":makeQuery(id+"F1MoAnU7Y2teXVl_2.5.F4.boolean.opBoolean","SPLIT",FACE,{"disambiguationData":[TD([subQ3])],"derivedFrom":makeQuery(id+"F1MoAnU7Y2teXVl_2.4.F4.boolean.opBoolean","SPLIT",FACE,{"disambiguationData":[TD([subQ3])],"derivedFrom":makeQuery(id+"F1MoAnU7Y2teXVl_2.3.F4.boolean.opBoolean","SPLIT",FACE,{"disambiguationData":[TD([subQ3])],"derivedFrom":makeQuery(id+"F1MoAnU7Y2teXVl_2.2.F4.boolean.opBoolean","SPLIT",FACE,{"disambiguationData":[TD([subQ3])],"derivedFrom":makeQuery(id+"F1MoAnU7Y2teXVl_2.1.F4.boolean.opBoolean","SPLIT",FACE,{"disambiguationData":[TD([subQ3])],"derivedFrom":makeQuery(id+"F3.opRevolve","SWEPT_FACE",FACE,{"disambiguationData":[OSD([sQuery(id+"F0.wireOp",EDGE,"E34")])]})})})})})})})})})})})})})})}),makeQuery(id+"F1MoAnU7Y2teXVl_2.15.F4.opExtrude","SWEPT_FACE",FACE,{"disambiguationData":[OSD([subQ0])]})]});}
            var Q16;
            {var subQ0=sQuery(id+"F1.wireOp",EDGE,"E61");Q16=makeQuery(id+"F1MoAnU7Y2teXVl_2.2.F4.boolean.opBoolean","INTERSECT",EDGE,{"derivedFrom":[makeQuery(id+"F1MoAnU7Y2teXVl_2.1.F4.boolean.opBoolean","SPLIT",FACE,{"disambiguationData":[TD([makeQuery(id+"F4.boolean.opBoolean","COPY",FACE,{"derivedFrom":makeQuery(id+"F4.opExtrude","SWEPT_FACE",FACE,{"disambiguationData":[OSD([sQuery(id+"F1.wireOp",EDGE,"E62")])]})})])],"derivedFrom":makeQuery(id+"F3.opRevolve","SWEPT_FACE",FACE,{"disambiguationData":[OSD([sQuery(id+"F0.wireOp",EDGE,"E30")])]})}),makeQuery(id+"F1MoAnU7Y2teXVl_2.2.F4.opExtrude","SWEPT_FACE",FACE,{"disambiguationData":[OSD([subQ0])]})]});}
            var Q17;
            Q17=makeQuery(id+"F1MoAnU7Y2teXVl_2.1.F4.boolean.opBoolean","INTERSECT",EDGE,{"derivedFrom":[makeQuery(id+"F3.opRevolve","SWEPT_FACE",FACE,{"disambiguationData":[OSD([sQuery(id+"F0.wireOp",EDGE,"E30")])]}),makeQuery(id+"F1MoAnU7Y2teXVl_2.1.F4.opExtrude","SWEPT_FACE",FACE,{"disambiguationData":[OSD([sQuery(id+"F1.wireOp",EDGE,"E61")])]})]});
            var Q18;
            Q18=makeQuery(id+"F4.boolean.opBoolean","INTERSECT",EDGE,{"derivedFrom":[makeQuery(id+"F3.opRevolve","SWEPT_FACE",FACE,{"disambiguationData":[OSD([sQuery(id+"F0.wireOp",EDGE,"E30")])]}),makeQuery(id+"F4.opExtrude","SWEPT_FACE",FACE,{"disambiguationData":[OSD([sQuery(id+"F1.wireOp",EDGE,"E61")])]})]});
            var Q19;
            {var subQ0=sQuery(id+"F1.wireOp",EDGE,"E61");var subQ3=makeQuery(id+"F4.boolean.opBoolean","COPY",FACE,{"derivedFrom":makeQuery(id+"F4.opExtrude","SWEPT_FACE",FACE,{"disambiguationData":[OSD([sQuery(id+"F1.wireOp",EDGE,"E62")])]})});Q19=makeQuery(id+"F1MoAnU7Y2teXVl_2.15.F4.boolean.opBoolean","INTERSECT",EDGE,{"derivedFrom":[makeQuery(id+"F1MoAnU7Y2teXVl_2.14.F4.boolean.opBoolean","SPLIT",FACE,{"disambiguationData":[TD([subQ3])],"derivedFrom":makeQuery(id+"F1MoAnU7Y2teXVl_2.13.F4.boolean.opBoolean","SPLIT",FACE,{"disambiguationData":[TD([subQ3])],"derivedFrom":makeQuery(id+"F1MoAnU7Y2teXVl_2.12.F4.boolean.opBoolean","SPLIT",FACE,{"disambiguationData":[TD([subQ3])],"derivedFrom":makeQuery(id+"F1MoAnU7Y2teXVl_2.11.F4.boolean.opBoolean","SPLIT",FACE,{"disambiguationData":[TD([subQ3])],"derivedFrom":makeQuery(id+"F1MoAnU7Y2teXVl_2.10.F4.boolean.opBoolean","SPLIT",FACE,{"disambiguationData":[TD([subQ3])],"derivedFrom":makeQuery(id+"F1MoAnU7Y2teXVl_2.9.F4.boolean.opBoolean","SPLIT",FACE,{"disambiguationData":[TD([subQ3])],"derivedFrom":makeQuery(id+"F1MoAnU7Y2teXVl_2.8.F4.boolean.opBoolean","SPLIT",FACE,{"disambiguationData":[TD([subQ3])],"derivedFrom":makeQuery(id+"F1MoAnU7Y2teXVl_2.7.F4.boolean.opBoolean","SPLIT",FACE,{"disambiguationData":[TD([subQ3])],"derivedFrom":makeQuery(id+"F1MoAnU7Y2teXVl_2.6.F4.boolean.opBoolean","SPLIT",FACE,{"disambiguationData":[TD([subQ3])],"derivedFrom":makeQuery(id+"F1MoAnU7Y2teXVl_2.5.F4.boolean.opBoolean","SPLIT",FACE,{"disambiguationData":[TD([subQ3])],"derivedFrom":makeQuery(id+"F1MoAnU7Y2teXVl_2.4.F4.boolean.opBoolean","SPLIT",FACE,{"disambiguationData":[TD([subQ3])],"derivedFrom":makeQuery(id+"F1MoAnU7Y2teXVl_2.3.F4.boolean.opBoolean","SPLIT",FACE,{"disambiguationData":[TD([subQ3])],"derivedFrom":makeQuery(id+"F1MoAnU7Y2teXVl_2.2.F4.boolean.opBoolean","SPLIT",FACE,{"disambiguationData":[TD([subQ3])],"derivedFrom":makeQuery(id+"F1MoAnU7Y2teXVl_2.1.F4.boolean.opBoolean","SPLIT",FACE,{"disambiguationData":[TD([subQ3])],"derivedFrom":makeQuery(id+"F3.opRevolve","SWEPT_FACE",FACE,{"disambiguationData":[OSD([sQuery(id+"F0.wireOp",EDGE,"E30")])]})})})})})})})})})})})})})})}),makeQuery(id+"F1MoAnU7Y2teXVl_2.15.F4.opExtrude","SWEPT_FACE",FACE,{"disambiguationData":[OSD([subQ0])]})]});}
            var Q20;
            {var subQ0=sQuery(id+"F1.wireOp",EDGE,"E61");var subQ3=makeQuery(id+"F4.boolean.opBoolean","COPY",FACE,{"derivedFrom":makeQuery(id+"F4.opExtrude","SWEPT_FACE",FACE,{"disambiguationData":[OSD([sQuery(id+"F1.wireOp",EDGE,"E62")])]})});Q20=makeQuery(id+"F1MoAnU7Y2teXVl_2.14.F4.boolean.opBoolean","INTERSECT",EDGE,{"derivedFrom":[makeQuery(id+"F1MoAnU7Y2teXVl_2.13.F4.boolean.opBoolean","SPLIT",FACE,{"disambiguationData":[TD([subQ3])],"derivedFrom":makeQuery(id+"F1MoAnU7Y2teXVl_2.12.F4.boolean.opBoolean","SPLIT",FACE,{"disambiguationData":[TD([subQ3])],"derivedFrom":makeQuery(id+"F1MoAnU7Y2teXVl_2.11.F4.boolean.opBoolean","SPLIT",FACE,{"disambiguationData":[TD([subQ3])],"derivedFrom":makeQuery(id+"F1MoAnU7Y2teXVl_2.10.F4.boolean.opBoolean","SPLIT",FACE,{"disambiguationData":[TD([subQ3])],"derivedFrom":makeQuery(id+"F1MoAnU7Y2teXVl_2.9.F4.boolean.opBoolean","SPLIT",FACE,{"disambiguationData":[TD([subQ3])],"derivedFrom":makeQuery(id+"F1MoAnU7Y2teXVl_2.8.F4.boolean.opBoolean","SPLIT",FACE,{"disambiguationData":[TD([subQ3])],"derivedFrom":makeQuery(id+"F1MoAnU7Y2teXVl_2.7.F4.boolean.opBoolean","SPLIT",FACE,{"disambiguationData":[TD([subQ3])],"derivedFrom":makeQuery(id+"F1MoAnU7Y2teXVl_2.6.F4.boolean.opBoolean","SPLIT",FACE,{"disambiguationData":[TD([subQ3])],"derivedFrom":makeQuery(id+"F1MoAnU7Y2teXVl_2.5.F4.boolean.opBoolean","SPLIT",FACE,{"disambiguationData":[TD([subQ3])],"derivedFrom":makeQuery(id+"F1MoAnU7Y2teXVl_2.4.F4.boolean.opBoolean","SPLIT",FACE,{"disambiguationData":[TD([subQ3])],"derivedFrom":makeQuery(id+"F1MoAnU7Y2teXVl_2.3.F4.boolean.opBoolean","SPLIT",FACE,{"disambiguationData":[TD([subQ3])],"derivedFrom":makeQuery(id+"F1MoAnU7Y2teXVl_2.2.F4.boolean.opBoolean","SPLIT",FACE,{"disambiguationData":[TD([subQ3])],"derivedFrom":makeQuery(id+"F1MoAnU7Y2teXVl_2.1.F4.boolean.opBoolean","SPLIT",FACE,{"disambiguationData":[TD([subQ3])],"derivedFrom":makeQuery(id+"F3.opRevolve","SWEPT_FACE",FACE,{"disambiguationData":[OSD([sQuery(id+"F0.wireOp",EDGE,"E30")])]})})})})})})})})})})})})})}),makeQuery(id+"F1MoAnU7Y2teXVl_2.14.F4.opExtrude","SWEPT_FACE",FACE,{"disambiguationData":[OSD([subQ0])]})]});}
            var Q21;
            {var subQ0=sQuery(id+"F1.wireOp",EDGE,"E61");var subQ3=makeQuery(id+"F4.boolean.opBoolean","COPY",FACE,{"derivedFrom":makeQuery(id+"F4.opExtrude","SWEPT_FACE",FACE,{"disambiguationData":[OSD([sQuery(id+"F1.wireOp",EDGE,"E62")])]})});Q21=makeQuery(id+"F1MoAnU7Y2teXVl_2.13.F4.boolean.opBoolean","INTERSECT",EDGE,{"derivedFrom":[makeQuery(id+"F1MoAnU7Y2teXVl_2.12.F4.boolean.opBoolean","SPLIT",FACE,{"disambiguationData":[TD([subQ3])],"derivedFrom":makeQuery(id+"F1MoAnU7Y2teXVl_2.11.F4.boolean.opBoolean","SPLIT",FACE,{"disambiguationData":[TD([subQ3])],"derivedFrom":makeQuery(id+"F1MoAnU7Y2teXVl_2.10.F4.boolean.opBoolean","SPLIT",FACE,{"disambiguationData":[TD([subQ3])],"derivedFrom":makeQuery(id+"F1MoAnU7Y2teXVl_2.9.F4.boolean.opBoolean","SPLIT",FACE,{"disambiguationData":[TD([subQ3])],"derivedFrom":makeQuery(id+"F1MoAnU7Y2teXVl_2.8.F4.boolean.opBoolean","SPLIT",FACE,{"disambiguationData":[TD([subQ3])],"derivedFrom":makeQuery(id+"F1MoAnU7Y2teXVl_2.7.F4.boolean.opBoolean","SPLIT",FACE,{"disambiguationData":[TD([subQ3])],"derivedFrom":makeQuery(id+"F1MoAnU7Y2teXVl_2.6.F4.boolean.opBoolean","SPLIT",FACE,{"disambiguationData":[TD([subQ3])],"derivedFrom":makeQuery(id+"F1MoAnU7Y2teXVl_2.5.F4.boolean.opBoolean","SPLIT",FACE,{"disambiguationData":[TD([subQ3])],"derivedFrom":makeQuery(id+"F1MoAnU7Y2teXVl_2.4.F4.boolean.opBoolean","SPLIT",FACE,{"disambiguationData":[TD([subQ3])],"derivedFrom":makeQuery(id+"F1MoAnU7Y2teXVl_2.3.F4.boolean.opBoolean","SPLIT",FACE,{"disambiguationData":[TD([subQ3])],"derivedFrom":makeQuery(id+"F1MoAnU7Y2teXVl_2.2.F4.boolean.opBoolean","SPLIT",FACE,{"disambiguationData":[TD([subQ3])],"derivedFrom":makeQuery(id+"F1MoAnU7Y2teXVl_2.1.F4.boolean.opBoolean","SPLIT",FACE,{"disambiguationData":[TD([subQ3])],"derivedFrom":makeQuery(id+"F3.opRevolve","SWEPT_FACE",FACE,{"disambiguationData":[OSD([sQuery(id+"F0.wireOp",EDGE,"E30")])]})})})})})})})})})})})})}),makeQuery(id+"F1MoAnU7Y2teXVl_2.13.F4.opExtrude","SWEPT_FACE",FACE,{"disambiguationData":[OSD([subQ0])]})]});}
            var Q22;
            {var subQ0=sQuery(id+"F1.wireOp",EDGE,"E61");var subQ3=makeQuery(id+"F4.boolean.opBoolean","COPY",FACE,{"derivedFrom":makeQuery(id+"F4.opExtrude","SWEPT_FACE",FACE,{"disambiguationData":[OSD([sQuery(id+"F1.wireOp",EDGE,"E62")])]})});Q22=makeQuery(id+"F1MoAnU7Y2teXVl_2.12.F4.boolean.opBoolean","INTERSECT",EDGE,{"derivedFrom":[makeQuery(id+"F1MoAnU7Y2teXVl_2.11.F4.boolean.opBoolean","SPLIT",FACE,{"disambiguationData":[TD([subQ3])],"derivedFrom":makeQuery(id+"F1MoAnU7Y2teXVl_2.10.F4.boolean.opBoolean","SPLIT",FACE,{"disambiguationData":[TD([subQ3])],"derivedFrom":makeQuery(id+"F1MoAnU7Y2teXVl_2.9.F4.boolean.opBoolean","SPLIT",FACE,{"disambiguationData":[TD([subQ3])],"derivedFrom":makeQuery(id+"F1MoAnU7Y2teXVl_2.8.F4.boolean.opBoolean","SPLIT",FACE,{"disambiguationData":[TD([subQ3])],"derivedFrom":makeQuery(id+"F1MoAnU7Y2teXVl_2.7.F4.boolean.opBoolean","SPLIT",FACE,{"disambiguationData":[TD([subQ3])],"derivedFrom":makeQuery(id+"F1MoAnU7Y2teXVl_2.6.F4.boolean.opBoolean","SPLIT",FACE,{"disambiguationData":[TD([subQ3])],"derivedFrom":makeQuery(id+"F1MoAnU7Y2teXVl_2.5.F4.boolean.opBoolean","SPLIT",FACE,{"disambiguationData":[TD([subQ3])],"derivedFrom":makeQuery(id+"F1MoAnU7Y2teXVl_2.4.F4.boolean.opBoolean","SPLIT",FACE,{"disambiguationData":[TD([subQ3])],"derivedFrom":makeQuery(id+"F1MoAnU7Y2teXVl_2.3.F4.boolean.opBoolean","SPLIT",FACE,{"disambiguationData":[TD([subQ3])],"derivedFrom":makeQuery(id+"F1MoAnU7Y2teXVl_2.2.F4.boolean.opBoolean","SPLIT",FACE,{"disambiguationData":[TD([subQ3])],"derivedFrom":makeQuery(id+"F1MoAnU7Y2teXVl_2.1.F4.boolean.opBoolean","SPLIT",FACE,{"disambiguationData":[TD([subQ3])],"derivedFrom":makeQuery(id+"F3.opRevolve","SWEPT_FACE",FACE,{"disambiguationData":[OSD([sQuery(id+"F0.wireOp",EDGE,"E30")])]})})})})})})})})})})})}),makeQuery(id+"F1MoAnU7Y2teXVl_2.12.F4.opExtrude","SWEPT_FACE",FACE,{"disambiguationData":[OSD([subQ0])]})]});}
            var Q23;
            {var subQ0=sQuery(id+"F1.wireOp",EDGE,"E61");var subQ3=makeQuery(id+"F4.boolean.opBoolean","COPY",FACE,{"derivedFrom":makeQuery(id+"F4.opExtrude","SWEPT_FACE",FACE,{"disambiguationData":[OSD([sQuery(id+"F1.wireOp",EDGE,"E62")])]})});Q23=makeQuery(id+"F1MoAnU7Y2teXVl_2.11.F4.boolean.opBoolean","INTERSECT",EDGE,{"derivedFrom":[makeQuery(id+"F1MoAnU7Y2teXVl_2.10.F4.boolean.opBoolean","SPLIT",FACE,{"disambiguationData":[TD([subQ3])],"derivedFrom":makeQuery(id+"F1MoAnU7Y2teXVl_2.9.F4.boolean.opBoolean","SPLIT",FACE,{"disambiguationData":[TD([subQ3])],"derivedFrom":makeQuery(id+"F1MoAnU7Y2teXVl_2.8.F4.boolean.opBoolean","SPLIT",FACE,{"disambiguationData":[TD([subQ3])],"derivedFrom":makeQuery(id+"F1MoAnU7Y2teXVl_2.7.F4.boolean.opBoolean","SPLIT",FACE,{"disambiguationData":[TD([subQ3])],"derivedFrom":makeQuery(id+"F1MoAnU7Y2teXVl_2.6.F4.boolean.opBoolean","SPLIT",FACE,{"disambiguationData":[TD([subQ3])],"derivedFrom":makeQuery(id+"F1MoAnU7Y2teXVl_2.5.F4.boolean.opBoolean","SPLIT",FACE,{"disambiguationData":[TD([subQ3])],"derivedFrom":makeQuery(id+"F1MoAnU7Y2teXVl_2.4.F4.boolean.opBoolean","SPLIT",FACE,{"disambiguationData":[TD([subQ3])],"derivedFrom":makeQuery(id+"F1MoAnU7Y2teXVl_2.3.F4.boolean.opBoolean","SPLIT",FACE,{"disambiguationData":[TD([subQ3])],"derivedFrom":makeQuery(id+"F1MoAnU7Y2teXVl_2.2.F4.boolean.opBoolean","SPLIT",FACE,{"disambiguationData":[TD([subQ3])],"derivedFrom":makeQuery(id+"F1MoAnU7Y2teXVl_2.1.F4.boolean.opBoolean","SPLIT",FACE,{"disambiguationData":[TD([subQ3])],"derivedFrom":makeQuery(id+"F3.opRevolve","SWEPT_FACE",FACE,{"disambiguationData":[OSD([sQuery(id+"F0.wireOp",EDGE,"E30")])]})})})})})})})})})})}),makeQuery(id+"F1MoAnU7Y2teXVl_2.11.F4.opExtrude","SWEPT_FACE",FACE,{"disambiguationData":[OSD([subQ0])]})]});}
            var Q24;
            {var subQ0=sQuery(id+"F1.wireOp",EDGE,"E61");var subQ3=makeQuery(id+"F4.boolean.opBoolean","COPY",FACE,{"derivedFrom":makeQuery(id+"F4.opExtrude","SWEPT_FACE",FACE,{"disambiguationData":[OSD([sQuery(id+"F1.wireOp",EDGE,"E62")])]})});Q24=makeQuery(id+"F1MoAnU7Y2teXVl_2.10.F4.boolean.opBoolean","INTERSECT",EDGE,{"derivedFrom":[makeQuery(id+"F1MoAnU7Y2teXVl_2.9.F4.boolean.opBoolean","SPLIT",FACE,{"disambiguationData":[TD([subQ3])],"derivedFrom":makeQuery(id+"F1MoAnU7Y2teXVl_2.8.F4.boolean.opBoolean","SPLIT",FACE,{"disambiguationData":[TD([subQ3])],"derivedFrom":makeQuery(id+"F1MoAnU7Y2teXVl_2.7.F4.boolean.opBoolean","SPLIT",FACE,{"disambiguationData":[TD([subQ3])],"derivedFrom":makeQuery(id+"F1MoAnU7Y2teXVl_2.6.F4.boolean.opBoolean","SPLIT",FACE,{"disambiguationData":[TD([subQ3])],"derivedFrom":makeQuery(id+"F1MoAnU7Y2teXVl_2.5.F4.boolean.opBoolean","SPLIT",FACE,{"disambiguationData":[TD([subQ3])],"derivedFrom":makeQuery(id+"F1MoAnU7Y2teXVl_2.4.F4.boolean.opBoolean","SPLIT",FACE,{"disambiguationData":[TD([subQ3])],"derivedFrom":makeQuery(id+"F1MoAnU7Y2teXVl_2.3.F4.boolean.opBoolean","SPLIT",FACE,{"disambiguationData":[TD([subQ3])],"derivedFrom":makeQuery(id+"F1MoAnU7Y2teXVl_2.2.F4.boolean.opBoolean","SPLIT",FACE,{"disambiguationData":[TD([subQ3])],"derivedFrom":makeQuery(id+"F1MoAnU7Y2teXVl_2.1.F4.boolean.opBoolean","SPLIT",FACE,{"disambiguationData":[TD([subQ3])],"derivedFrom":makeQuery(id+"F3.opRevolve","SWEPT_FACE",FACE,{"disambiguationData":[OSD([sQuery(id+"F0.wireOp",EDGE,"E30")])]})})})})})})})})})}),makeQuery(id+"F1MoAnU7Y2teXVl_2.10.F4.opExtrude","SWEPT_FACE",FACE,{"disambiguationData":[OSD([subQ0])]})]});}
            var Q25;
            {var subQ0=sQuery(id+"F1.wireOp",EDGE,"E61");var subQ3=makeQuery(id+"F4.boolean.opBoolean","COPY",FACE,{"derivedFrom":makeQuery(id+"F4.opExtrude","SWEPT_FACE",FACE,{"disambiguationData":[OSD([sQuery(id+"F1.wireOp",EDGE,"E62")])]})});Q25=makeQuery(id+"F1MoAnU7Y2teXVl_2.9.F4.boolean.opBoolean","INTERSECT",EDGE,{"derivedFrom":[makeQuery(id+"F1MoAnU7Y2teXVl_2.8.F4.boolean.opBoolean","SPLIT",FACE,{"disambiguationData":[TD([subQ3])],"derivedFrom":makeQuery(id+"F1MoAnU7Y2teXVl_2.7.F4.boolean.opBoolean","SPLIT",FACE,{"disambiguationData":[TD([subQ3])],"derivedFrom":makeQuery(id+"F1MoAnU7Y2teXVl_2.6.F4.boolean.opBoolean","SPLIT",FACE,{"disambiguationData":[TD([subQ3])],"derivedFrom":makeQuery(id+"F1MoAnU7Y2teXVl_2.5.F4.boolean.opBoolean","SPLIT",FACE,{"disambiguationData":[TD([subQ3])],"derivedFrom":makeQuery(id+"F1MoAnU7Y2teXVl_2.4.F4.boolean.opBoolean","SPLIT",FACE,{"disambiguationData":[TD([subQ3])],"derivedFrom":makeQuery(id+"F1MoAnU7Y2teXVl_2.3.F4.boolean.opBoolean","SPLIT",FACE,{"disambiguationData":[TD([subQ3])],"derivedFrom":makeQuery(id+"F1MoAnU7Y2teXVl_2.2.F4.boolean.opBoolean","SPLIT",FACE,{"disambiguationData":[TD([subQ3])],"derivedFrom":makeQuery(id+"F1MoAnU7Y2teXVl_2.1.F4.boolean.opBoolean","SPLIT",FACE,{"disambiguationData":[TD([subQ3])],"derivedFrom":makeQuery(id+"F3.opRevolve","SWEPT_FACE",FACE,{"disambiguationData":[OSD([sQuery(id+"F0.wireOp",EDGE,"E30")])]})})})})})})})})}),makeQuery(id+"F1MoAnU7Y2teXVl_2.9.F4.opExtrude","SWEPT_FACE",FACE,{"disambiguationData":[OSD([subQ0])]})]});}
            var Q26;
            {var subQ0=sQuery(id+"F1.wireOp",EDGE,"E61");var subQ3=makeQuery(id+"F4.boolean.opBoolean","COPY",FACE,{"derivedFrom":makeQuery(id+"F4.opExtrude","SWEPT_FACE",FACE,{"disambiguationData":[OSD([sQuery(id+"F1.wireOp",EDGE,"E62")])]})});Q26=makeQuery(id+"F1MoAnU7Y2teXVl_2.8.F4.boolean.opBoolean","INTERSECT",EDGE,{"derivedFrom":[makeQuery(id+"F1MoAnU7Y2teXVl_2.7.F4.boolean.opBoolean","SPLIT",FACE,{"disambiguationData":[TD([subQ3])],"derivedFrom":makeQuery(id+"F1MoAnU7Y2teXVl_2.6.F4.boolean.opBoolean","SPLIT",FACE,{"disambiguationData":[TD([subQ3])],"derivedFrom":makeQuery(id+"F1MoAnU7Y2teXVl_2.5.F4.boolean.opBoolean","SPLIT",FACE,{"disambiguationData":[TD([subQ3])],"derivedFrom":makeQuery(id+"F1MoAnU7Y2teXVl_2.4.F4.boolean.opBoolean","SPLIT",FACE,{"disambiguationData":[TD([subQ3])],"derivedFrom":makeQuery(id+"F1MoAnU7Y2teXVl_2.3.F4.boolean.opBoolean","SPLIT",FACE,{"disambiguationData":[TD([subQ3])],"derivedFrom":makeQuery(id+"F1MoAnU7Y2teXVl_2.2.F4.boolean.opBoolean","SPLIT",FACE,{"disambiguationData":[TD([subQ3])],"derivedFrom":makeQuery(id+"F1MoAnU7Y2teXVl_2.1.F4.boolean.opBoolean","SPLIT",FACE,{"disambiguationData":[TD([subQ3])],"derivedFrom":makeQuery(id+"F3.opRevolve","SWEPT_FACE",FACE,{"disambiguationData":[OSD([sQuery(id+"F0.wireOp",EDGE,"E30")])]})})})})})})})}),makeQuery(id+"F1MoAnU7Y2teXVl_2.8.F4.opExtrude","SWEPT_FACE",FACE,{"disambiguationData":[OSD([subQ0])]})]});}
            var Q27;
            {var subQ0=sQuery(id+"F1.wireOp",EDGE,"E61");var subQ3=makeQuery(id+"F4.boolean.opBoolean","COPY",FACE,{"derivedFrom":makeQuery(id+"F4.opExtrude","SWEPT_FACE",FACE,{"disambiguationData":[OSD([sQuery(id+"F1.wireOp",EDGE,"E62")])]})});Q27=makeQuery(id+"F1MoAnU7Y2teXVl_2.7.F4.boolean.opBoolean","INTERSECT",EDGE,{"derivedFrom":[makeQuery(id+"F1MoAnU7Y2teXVl_2.6.F4.boolean.opBoolean","SPLIT",FACE,{"disambiguationData":[TD([subQ3])],"derivedFrom":makeQuery(id+"F1MoAnU7Y2teXVl_2.5.F4.boolean.opBoolean","SPLIT",FACE,{"disambiguationData":[TD([subQ3])],"derivedFrom":makeQuery(id+"F1MoAnU7Y2teXVl_2.4.F4.boolean.opBoolean","SPLIT",FACE,{"disambiguationData":[TD([subQ3])],"derivedFrom":makeQuery(id+"F1MoAnU7Y2teXVl_2.3.F4.boolean.opBoolean","SPLIT",FACE,{"disambiguationData":[TD([subQ3])],"derivedFrom":makeQuery(id+"F1MoAnU7Y2teXVl_2.2.F4.boolean.opBoolean","SPLIT",FACE,{"disambiguationData":[TD([subQ3])],"derivedFrom":makeQuery(id+"F1MoAnU7Y2teXVl_2.1.F4.boolean.opBoolean","SPLIT",FACE,{"disambiguationData":[TD([subQ3])],"derivedFrom":makeQuery(id+"F3.opRevolve","SWEPT_FACE",FACE,{"disambiguationData":[OSD([sQuery(id+"F0.wireOp",EDGE,"E30")])]})})})})})})}),makeQuery(id+"F1MoAnU7Y2teXVl_2.7.F4.opExtrude","SWEPT_FACE",FACE,{"disambiguationData":[OSD([subQ0])]})]});}
            var Q28;
            {var subQ0=sQuery(id+"F1.wireOp",EDGE,"E61");var subQ3=makeQuery(id+"F4.boolean.opBoolean","COPY",FACE,{"derivedFrom":makeQuery(id+"F4.opExtrude","SWEPT_FACE",FACE,{"disambiguationData":[OSD([sQuery(id+"F1.wireOp",EDGE,"E62")])]})});Q28=makeQuery(id+"F1MoAnU7Y2teXVl_2.6.F4.boolean.opBoolean","INTERSECT",EDGE,{"derivedFrom":[makeQuery(id+"F1MoAnU7Y2teXVl_2.5.F4.boolean.opBoolean","SPLIT",FACE,{"disambiguationData":[TD([subQ3])],"derivedFrom":makeQuery(id+"F1MoAnU7Y2teXVl_2.4.F4.boolean.opBoolean","SPLIT",FACE,{"disambiguationData":[TD([subQ3])],"derivedFrom":makeQuery(id+"F1MoAnU7Y2teXVl_2.3.F4.boolean.opBoolean","SPLIT",FACE,{"disambiguationData":[TD([subQ3])],"derivedFrom":makeQuery(id+"F1MoAnU7Y2teXVl_2.2.F4.boolean.opBoolean","SPLIT",FACE,{"disambiguationData":[TD([subQ3])],"derivedFrom":makeQuery(id+"F1MoAnU7Y2teXVl_2.1.F4.boolean.opBoolean","SPLIT",FACE,{"disambiguationData":[TD([subQ3])],"derivedFrom":makeQuery(id+"F3.opRevolve","SWEPT_FACE",FACE,{"disambiguationData":[OSD([sQuery(id+"F0.wireOp",EDGE,"E30")])]})})})})})}),makeQuery(id+"F1MoAnU7Y2teXVl_2.6.F4.opExtrude","SWEPT_FACE",FACE,{"disambiguationData":[OSD([subQ0])]})]});}
            var Q29;
            {var subQ0=sQuery(id+"F1.wireOp",EDGE,"E61");var subQ3=makeQuery(id+"F4.boolean.opBoolean","COPY",FACE,{"derivedFrom":makeQuery(id+"F4.opExtrude","SWEPT_FACE",FACE,{"disambiguationData":[OSD([sQuery(id+"F1.wireOp",EDGE,"E62")])]})});Q29=makeQuery(id+"F1MoAnU7Y2teXVl_2.5.F4.boolean.opBoolean","INTERSECT",EDGE,{"derivedFrom":[makeQuery(id+"F1MoAnU7Y2teXVl_2.4.F4.boolean.opBoolean","SPLIT",FACE,{"disambiguationData":[TD([subQ3])],"derivedFrom":makeQuery(id+"F1MoAnU7Y2teXVl_2.3.F4.boolean.opBoolean","SPLIT",FACE,{"disambiguationData":[TD([subQ3])],"derivedFrom":makeQuery(id+"F1MoAnU7Y2teXVl_2.2.F4.boolean.opBoolean","SPLIT",FACE,{"disambiguationData":[TD([subQ3])],"derivedFrom":makeQuery(id+"F1MoAnU7Y2teXVl_2.1.F4.boolean.opBoolean","SPLIT",FACE,{"disambiguationData":[TD([subQ3])],"derivedFrom":makeQuery(id+"F3.opRevolve","SWEPT_FACE",FACE,{"disambiguationData":[OSD([sQuery(id+"F0.wireOp",EDGE,"E30")])]})})})})}),makeQuery(id+"F1MoAnU7Y2teXVl_2.5.F4.opExtrude","SWEPT_FACE",FACE,{"disambiguationData":[OSD([subQ0])]})]});}
            var Q30;
            {var subQ0=sQuery(id+"F1.wireOp",EDGE,"E61");var subQ3=makeQuery(id+"F4.boolean.opBoolean","COPY",FACE,{"derivedFrom":makeQuery(id+"F4.opExtrude","SWEPT_FACE",FACE,{"disambiguationData":[OSD([sQuery(id+"F1.wireOp",EDGE,"E62")])]})});Q30=makeQuery(id+"F1MoAnU7Y2teXVl_2.4.F4.boolean.opBoolean","INTERSECT",EDGE,{"derivedFrom":[makeQuery(id+"F1MoAnU7Y2teXVl_2.3.F4.boolean.opBoolean","SPLIT",FACE,{"disambiguationData":[TD([subQ3])],"derivedFrom":makeQuery(id+"F1MoAnU7Y2teXVl_2.2.F4.boolean.opBoolean","SPLIT",FACE,{"disambiguationData":[TD([subQ3])],"derivedFrom":makeQuery(id+"F1MoAnU7Y2teXVl_2.1.F4.boolean.opBoolean","SPLIT",FACE,{"disambiguationData":[TD([subQ3])],"derivedFrom":makeQuery(id+"F3.opRevolve","SWEPT_FACE",FACE,{"disambiguationData":[OSD([sQuery(id+"F0.wireOp",EDGE,"E30")])]})})})}),makeQuery(id+"F1MoAnU7Y2teXVl_2.4.F4.opExtrude","SWEPT_FACE",FACE,{"disambiguationData":[OSD([subQ0])]})]});}
            var Q31;
            {var subQ0=sQuery(id+"F1.wireOp",EDGE,"E61");var subQ3=makeQuery(id+"F4.boolean.opBoolean","COPY",FACE,{"derivedFrom":makeQuery(id+"F4.opExtrude","SWEPT_FACE",FACE,{"disambiguationData":[OSD([sQuery(id+"F1.wireOp",EDGE,"E62")])]})});Q31=makeQuery(id+"F1MoAnU7Y2teXVl_2.3.F4.boolean.opBoolean","INTERSECT",EDGE,{"derivedFrom":[makeQuery(id+"F1MoAnU7Y2teXVl_2.2.F4.boolean.opBoolean","SPLIT",FACE,{"disambiguationData":[TD([subQ3])],"derivedFrom":makeQuery(id+"F1MoAnU7Y2teXVl_2.1.F4.boolean.opBoolean","SPLIT",FACE,{"disambiguationData":[TD([subQ3])],"derivedFrom":makeQuery(id+"F3.opRevolve","SWEPT_FACE",FACE,{"disambiguationData":[OSD([sQuery(id+"F0.wireOp",EDGE,"E30")])]})})}),makeQuery(id+"F1MoAnU7Y2teXVl_2.3.F4.opExtrude","SWEPT_FACE",FACE,{"disambiguationData":[OSD([subQ0])]})]});}
            fillet(context, id + "F5", {"entities" : qUnion([Q0, Q1, Q2, Q3, Q4, Q5, Q6, Q7, Q8, Q9, Q10, Q11, Q12, Q13, Q14, Q15, Q16, Q17, Q18, Q19, Q20, Q21, Q22, Q23, Q24, Q25, Q26, Q27, Q28, Q29, Q30, Q31]), "radius" : 2 * mm, "tangentPropagation" : true, "allowEdgeOverflow" : false});
        }
        {
            var Q0;
            {var subQ0=sQuery(id+"F0.wireOp",EDGE,"E2");var subQ2=sQuery(id+"F1.wireOp",EDGE,"E62");var subQ3=sQuery(id+"F0.wireOp",EDGE,"E29");var subQ5=sQuery(id+"F1.wireOp",EDGE,"E61");var subQ6=makeQuery(id+"F1MoAnU7Y2teXVl_2.8.F4.opExtrude","SWEPT_FACE",FACE,{"disambiguationData":[OSD([subQ5])]});var subQ7=makeQuery(id+"F4.boolean.opBoolean","COPY",FACE,{"derivedFrom":makeQuery(id+"F4.opExtrude","SWEPT_FACE",FACE,{"disambiguationData":[OSD([subQ2])]})});Q0=makeQuery(id+"F1MoAnU7Y2teXVl_2.9.F4.boolean.opBoolean","SPLIT",EDGE,{"disambiguationData":[TD([makeQuery(id+"F1MoAnU7Y2teXVl_2.8.F4.boolean.opBoolean","COPY",FACE,{"derivedFrom":subQ6})])],"derivedFrom":makeQuery(id+"F1MoAnU7Y2teXVl_2.8.F4.boolean.opBoolean","SPLIT",EDGE,{"disambiguationData":[TD([subQ7])],"derivedFrom":makeQuery(id+"F1MoAnU7Y2teXVl_2.7.F4.boolean.opBoolean","SPLIT",EDGE,{"disambiguationData":[TD([subQ7])],"derivedFrom":makeQuery(id+"F1MoAnU7Y2teXVl_2.6.F4.boolean.opBoolean","SPLIT",EDGE,{"disambiguationData":[TD([subQ7])],"derivedFrom":makeQuery(id+"F1MoAnU7Y2teXVl_2.5.F4.boolean.opBoolean","SPLIT",EDGE,{"disambiguationData":[TD([subQ7])],"derivedFrom":makeQuery(id+"F1MoAnU7Y2teXVl_2.4.F4.boolean.opBoolean","SPLIT",EDGE,{"disambiguationData":[TD([subQ7])],"derivedFrom":makeQuery(id+"F1MoAnU7Y2teXVl_2.3.F4.boolean.opBoolean","SPLIT",EDGE,{"disambiguationData":[TD([subQ7])],"derivedFrom":makeQuery(id+"F1MoAnU7Y2teXVl_2.2.F4.boolean.opBoolean","SPLIT",EDGE,{"disambiguationData":[TD([subQ7])],"derivedFrom":makeQuery(id+"F1MoAnU7Y2teXVl_2.1.F4.boolean.opBoolean","SPLIT",EDGE,{"disambiguationData":[TD([subQ7])],"derivedFrom":makeQuery(id+"F3.opRevolve","SWEPT_EDGE",EDGE,{"disambiguationData":[OSD([subQ0,subQ3])]})})})})})})})})})});}
            var Q1;
            {var subQ0=sQuery(id+"F0.wireOp",EDGE,"E2");var subQ2=sQuery(id+"F0.wireOp",EDGE,"E29");var subQ4=makeQuery(id+"F4.boolean.opBoolean","COPY",FACE,{"derivedFrom":makeQuery(id+"F4.opExtrude","SWEPT_FACE",FACE,{"disambiguationData":[OSD([sQuery(id+"F1.wireOp",EDGE,"E62")])]})});Q1=makeQuery(id+"F1MoAnU7Y2teXVl_2.9.F4.boolean.opBoolean","SPLIT",EDGE,{"disambiguationData":[TD([subQ4])],"derivedFrom":makeQuery(id+"F1MoAnU7Y2teXVl_2.8.F4.boolean.opBoolean","SPLIT",EDGE,{"disambiguationData":[TD([subQ4])],"derivedFrom":makeQuery(id+"F1MoAnU7Y2teXVl_2.7.F4.boolean.opBoolean","SPLIT",EDGE,{"disambiguationData":[TD([subQ4])],"derivedFrom":makeQuery(id+"F1MoAnU7Y2teXVl_2.6.F4.boolean.opBoolean","SPLIT",EDGE,{"disambiguationData":[TD([subQ4])],"derivedFrom":makeQuery(id+"F1MoAnU7Y2teXVl_2.5.F4.boolean.opBoolean","SPLIT",EDGE,{"disambiguationData":[TD([subQ4])],"derivedFrom":makeQuery(id+"F1MoAnU7Y2teXVl_2.4.F4.boolean.opBoolean","SPLIT",EDGE,{"disambiguationData":[TD([subQ4])],"derivedFrom":makeQuery(id+"F1MoAnU7Y2teXVl_2.3.F4.boolean.opBoolean","SPLIT",EDGE,{"disambiguationData":[TD([subQ4])],"derivedFrom":makeQuery(id+"F1MoAnU7Y2teXVl_2.2.F4.boolean.opBoolean","SPLIT",EDGE,{"disambiguationData":[TD([subQ4])],"derivedFrom":makeQuery(id+"F1MoAnU7Y2teXVl_2.1.F4.boolean.opBoolean","SPLIT",EDGE,{"disambiguationData":[TD([subQ4])],"derivedFrom":makeQuery(id+"F3.opRevolve","SWEPT_EDGE",EDGE,{"disambiguationData":[OSD([subQ0,subQ2])]})})})})})})})})})});}
            var Q2;
            {var subQ0=sQuery(id+"F0.wireOp",EDGE,"E2");var subQ1=sQuery(id+"F0.wireOp",EDGE,"E29");Q2=makeQuery(id+"F1MoAnU7Y2teXVl_2.1.F4.boolean.opBoolean","SPLIT",EDGE,{"disambiguationData":[TD([makeQuery(id+"F4.boolean.opBoolean","COPY",FACE,{"derivedFrom":makeQuery(id+"F4.opExtrude","SWEPT_FACE",FACE,{"disambiguationData":[OSD([sQuery(id+"F1.wireOp",EDGE,"E61")])]})})])],"derivedFrom":makeQuery(id+"F3.opRevolve","SWEPT_EDGE",EDGE,{"disambiguationData":[OSD([subQ0,subQ1])]})});}
            var Q3;
            {var subQ0=sQuery(id+"F0.wireOp",EDGE,"E2");var subQ2=sQuery(id+"F0.wireOp",EDGE,"E29");var subQ4=makeQuery(id+"F1MoAnU7Y2teXVl_2.1.F4.opExtrude","SWEPT_FACE",FACE,{"disambiguationData":[OSD([sQuery(id+"F1.wireOp",EDGE,"E61")])]});var subQ5=sQuery(id+"F1.wireOp",EDGE,"E62");Q3=makeQuery(id+"F1MoAnU7Y2teXVl_2.2.F4.boolean.opBoolean","SPLIT",EDGE,{"disambiguationData":[TD([makeQuery(id+"F1MoAnU7Y2teXVl_2.1.F4.boolean.opBoolean","COPY",FACE,{"derivedFrom":subQ4})])],"derivedFrom":makeQuery(id+"F1MoAnU7Y2teXVl_2.1.F4.boolean.opBoolean","SPLIT",EDGE,{"disambiguationData":[TD([makeQuery(id+"F4.boolean.opBoolean","COPY",FACE,{"derivedFrom":makeQuery(id+"F4.opExtrude","SWEPT_FACE",FACE,{"disambiguationData":[OSD([subQ5])]})})])],"derivedFrom":makeQuery(id+"F3.opRevolve","SWEPT_EDGE",EDGE,{"disambiguationData":[OSD([subQ0,subQ2])]})})});}
            var Q4;
            {var subQ0=sQuery(id+"F0.wireOp",EDGE,"E2");var subQ2=sQuery(id+"F0.wireOp",EDGE,"E29");var subQ4=sQuery(id+"F1.wireOp",EDGE,"E61");var subQ5=makeQuery(id+"F1MoAnU7Y2teXVl_2.2.F4.opExtrude","SWEPT_FACE",FACE,{"disambiguationData":[OSD([subQ4])]});var subQ6=sQuery(id+"F1.wireOp",EDGE,"E62");var subQ7=makeQuery(id+"F4.boolean.opBoolean","COPY",FACE,{"derivedFrom":makeQuery(id+"F4.opExtrude","SWEPT_FACE",FACE,{"disambiguationData":[OSD([subQ6])]})});Q4=makeQuery(id+"F1MoAnU7Y2teXVl_2.3.F4.boolean.opBoolean","SPLIT",EDGE,{"disambiguationData":[TD([makeQuery(id+"F1MoAnU7Y2teXVl_2.2.F4.boolean.opBoolean","COPY",FACE,{"derivedFrom":subQ5})])],"derivedFrom":makeQuery(id+"F1MoAnU7Y2teXVl_2.2.F4.boolean.opBoolean","SPLIT",EDGE,{"disambiguationData":[TD([subQ7])],"derivedFrom":makeQuery(id+"F1MoAnU7Y2teXVl_2.1.F4.boolean.opBoolean","SPLIT",EDGE,{"disambiguationData":[TD([subQ7])],"derivedFrom":makeQuery(id+"F3.opRevolve","SWEPT_EDGE",EDGE,{"disambiguationData":[OSD([subQ0,subQ2])]})})})});}
            var Q5;
            {var subQ0=sQuery(id+"F0.wireOp",EDGE,"E2");var subQ2=sQuery(id+"F0.wireOp",EDGE,"E29");var subQ4=sQuery(id+"F1.wireOp",EDGE,"E62");var subQ5=sQuery(id+"F1.wireOp",EDGE,"E61");var subQ6=makeQuery(id+"F1MoAnU7Y2teXVl_2.3.F4.opExtrude","SWEPT_FACE",FACE,{"disambiguationData":[OSD([subQ5])]});var subQ7=makeQuery(id+"F4.boolean.opBoolean","COPY",FACE,{"derivedFrom":makeQuery(id+"F4.opExtrude","SWEPT_FACE",FACE,{"disambiguationData":[OSD([subQ4])]})});Q5=makeQuery(id+"F1MoAnU7Y2teXVl_2.4.F4.boolean.opBoolean","SPLIT",EDGE,{"disambiguationData":[TD([makeQuery(id+"F1MoAnU7Y2teXVl_2.3.F4.boolean.opBoolean","COPY",FACE,{"derivedFrom":subQ6})])],"derivedFrom":makeQuery(id+"F1MoAnU7Y2teXVl_2.3.F4.boolean.opBoolean","SPLIT",EDGE,{"disambiguationData":[TD([subQ7])],"derivedFrom":makeQuery(id+"F1MoAnU7Y2teXVl_2.2.F4.boolean.opBoolean","SPLIT",EDGE,{"disambiguationData":[TD([subQ7])],"derivedFrom":makeQuery(id+"F1MoAnU7Y2teXVl_2.1.F4.boolean.opBoolean","SPLIT",EDGE,{"disambiguationData":[TD([subQ7])],"derivedFrom":makeQuery(id+"F3.opRevolve","SWEPT_EDGE",EDGE,{"disambiguationData":[OSD([subQ0,subQ2])]})})})})});}
            var Q6;
            {var subQ0=sQuery(id+"F0.wireOp",EDGE,"E2");var subQ2=sQuery(id+"F0.wireOp",EDGE,"E29");var subQ4=sQuery(id+"F1.wireOp",EDGE,"E61");var subQ5=makeQuery(id+"F1MoAnU7Y2teXVl_2.4.F4.opExtrude","SWEPT_FACE",FACE,{"disambiguationData":[OSD([subQ4])]});var subQ6=sQuery(id+"F1.wireOp",EDGE,"E62");var subQ7=makeQuery(id+"F4.boolean.opBoolean","COPY",FACE,{"derivedFrom":makeQuery(id+"F4.opExtrude","SWEPT_FACE",FACE,{"disambiguationData":[OSD([subQ6])]})});Q6=makeQuery(id+"F1MoAnU7Y2teXVl_2.5.F4.boolean.opBoolean","SPLIT",EDGE,{"disambiguationData":[TD([makeQuery(id+"F1MoAnU7Y2teXVl_2.4.F4.boolean.opBoolean","COPY",FACE,{"derivedFrom":subQ5})])],"derivedFrom":makeQuery(id+"F1MoAnU7Y2teXVl_2.4.F4.boolean.opBoolean","SPLIT",EDGE,{"disambiguationData":[TD([subQ7])],"derivedFrom":makeQuery(id+"F1MoAnU7Y2teXVl_2.3.F4.boolean.opBoolean","SPLIT",EDGE,{"disambiguationData":[TD([subQ7])],"derivedFrom":makeQuery(id+"F1MoAnU7Y2teXVl_2.2.F4.boolean.opBoolean","SPLIT",EDGE,{"disambiguationData":[TD([subQ7])],"derivedFrom":makeQuery(id+"F1MoAnU7Y2teXVl_2.1.F4.boolean.opBoolean","SPLIT",EDGE,{"disambiguationData":[TD([subQ7])],"derivedFrom":makeQuery(id+"F3.opRevolve","SWEPT_EDGE",EDGE,{"disambiguationData":[OSD([subQ0,subQ2])]})})})})})});}
            var Q7;
            {var subQ0=sQuery(id+"F0.wireOp",EDGE,"E2");var subQ2=sQuery(id+"F0.wireOp",EDGE,"E29");var subQ4=sQuery(id+"F1.wireOp",EDGE,"E61");var subQ5=makeQuery(id+"F1MoAnU7Y2teXVl_2.5.F4.opExtrude","SWEPT_FACE",FACE,{"disambiguationData":[OSD([subQ4])]});var subQ6=sQuery(id+"F1.wireOp",EDGE,"E62");var subQ7=makeQuery(id+"F4.boolean.opBoolean","COPY",FACE,{"derivedFrom":makeQuery(id+"F4.opExtrude","SWEPT_FACE",FACE,{"disambiguationData":[OSD([subQ6])]})});Q7=makeQuery(id+"F1MoAnU7Y2teXVl_2.6.F4.boolean.opBoolean","SPLIT",EDGE,{"disambiguationData":[TD([makeQuery(id+"F1MoAnU7Y2teXVl_2.5.F4.boolean.opBoolean","COPY",FACE,{"derivedFrom":subQ5})])],"derivedFrom":makeQuery(id+"F1MoAnU7Y2teXVl_2.5.F4.boolean.opBoolean","SPLIT",EDGE,{"disambiguationData":[TD([subQ7])],"derivedFrom":makeQuery(id+"F1MoAnU7Y2teXVl_2.4.F4.boolean.opBoolean","SPLIT",EDGE,{"disambiguationData":[TD([subQ7])],"derivedFrom":makeQuery(id+"F1MoAnU7Y2teXVl_2.3.F4.boolean.opBoolean","SPLIT",EDGE,{"disambiguationData":[TD([subQ7])],"derivedFrom":makeQuery(id+"F1MoAnU7Y2teXVl_2.2.F4.boolean.opBoolean","SPLIT",EDGE,{"disambiguationData":[TD([subQ7])],"derivedFrom":makeQuery(id+"F1MoAnU7Y2teXVl_2.1.F4.boolean.opBoolean","SPLIT",EDGE,{"disambiguationData":[TD([subQ7])],"derivedFrom":makeQuery(id+"F3.opRevolve","SWEPT_EDGE",EDGE,{"disambiguationData":[OSD([subQ0,subQ2])]})})})})})})});}
            var Q8;
            {var subQ0=sQuery(id+"F0.wireOp",EDGE,"E2");var subQ2=sQuery(id+"F1.wireOp",EDGE,"E62");var subQ3=sQuery(id+"F0.wireOp",EDGE,"E29");var subQ5=sQuery(id+"F1.wireOp",EDGE,"E61");var subQ6=makeQuery(id+"F1MoAnU7Y2teXVl_2.6.F4.opExtrude","SWEPT_FACE",FACE,{"disambiguationData":[OSD([subQ5])]});var subQ7=makeQuery(id+"F4.boolean.opBoolean","COPY",FACE,{"derivedFrom":makeQuery(id+"F4.opExtrude","SWEPT_FACE",FACE,{"disambiguationData":[OSD([subQ2])]})});Q8=makeQuery(id+"F1MoAnU7Y2teXVl_2.7.F4.boolean.opBoolean","SPLIT",EDGE,{"disambiguationData":[TD([makeQuery(id+"F1MoAnU7Y2teXVl_2.6.F4.boolean.opBoolean","COPY",FACE,{"derivedFrom":subQ6})])],"derivedFrom":makeQuery(id+"F1MoAnU7Y2teXVl_2.6.F4.boolean.opBoolean","SPLIT",EDGE,{"disambiguationData":[TD([subQ7])],"derivedFrom":makeQuery(id+"F1MoAnU7Y2teXVl_2.5.F4.boolean.opBoolean","SPLIT",EDGE,{"disambiguationData":[TD([subQ7])],"derivedFrom":makeQuery(id+"F1MoAnU7Y2teXVl_2.4.F4.boolean.opBoolean","SPLIT",EDGE,{"disambiguationData":[TD([subQ7])],"derivedFrom":makeQuery(id+"F1MoAnU7Y2teXVl_2.3.F4.boolean.opBoolean","SPLIT",EDGE,{"disambiguationData":[TD([subQ7])],"derivedFrom":makeQuery(id+"F1MoAnU7Y2teXVl_2.2.F4.boolean.opBoolean","SPLIT",EDGE,{"disambiguationData":[TD([subQ7])],"derivedFrom":makeQuery(id+"F1MoAnU7Y2teXVl_2.1.F4.boolean.opBoolean","SPLIT",EDGE,{"disambiguationData":[TD([subQ7])],"derivedFrom":makeQuery(id+"F3.opRevolve","SWEPT_EDGE",EDGE,{"disambiguationData":[OSD([subQ0,subQ3])]})})})})})})})});}
            var Q9;
            {var subQ0=sQuery(id+"F0.wireOp",EDGE,"E2");var subQ2=sQuery(id+"F1.wireOp",EDGE,"E61");var subQ3=makeQuery(id+"F1MoAnU7Y2teXVl_2.7.F4.opExtrude","SWEPT_FACE",FACE,{"disambiguationData":[OSD([subQ2])]});var subQ4=sQuery(id+"F0.wireOp",EDGE,"E29");var subQ6=sQuery(id+"F1.wireOp",EDGE,"E62");var subQ7=makeQuery(id+"F4.boolean.opBoolean","COPY",FACE,{"derivedFrom":makeQuery(id+"F4.opExtrude","SWEPT_FACE",FACE,{"disambiguationData":[OSD([subQ6])]})});Q9=makeQuery(id+"F1MoAnU7Y2teXVl_2.8.F4.boolean.opBoolean","SPLIT",EDGE,{"disambiguationData":[TD([makeQuery(id+"F1MoAnU7Y2teXVl_2.7.F4.boolean.opBoolean","COPY",FACE,{"derivedFrom":subQ3})])],"derivedFrom":makeQuery(id+"F1MoAnU7Y2teXVl_2.7.F4.boolean.opBoolean","SPLIT",EDGE,{"disambiguationData":[TD([subQ7])],"derivedFrom":makeQuery(id+"F1MoAnU7Y2teXVl_2.6.F4.boolean.opBoolean","SPLIT",EDGE,{"disambiguationData":[TD([subQ7])],"derivedFrom":makeQuery(id+"F1MoAnU7Y2teXVl_2.5.F4.boolean.opBoolean","SPLIT",EDGE,{"disambiguationData":[TD([subQ7])],"derivedFrom":makeQuery(id+"F1MoAnU7Y2teXVl_2.4.F4.boolean.opBoolean","SPLIT",EDGE,{"disambiguationData":[TD([subQ7])],"derivedFrom":makeQuery(id+"F1MoAnU7Y2teXVl_2.3.F4.boolean.opBoolean","SPLIT",EDGE,{"disambiguationData":[TD([subQ7])],"derivedFrom":makeQuery(id+"F1MoAnU7Y2teXVl_2.2.F4.boolean.opBoolean","SPLIT",EDGE,{"disambiguationData":[TD([subQ7])],"derivedFrom":makeQuery(id+"F1MoAnU7Y2teXVl_2.1.F4.boolean.opBoolean","SPLIT",EDGE,{"disambiguationData":[TD([subQ7])],"derivedFrom":makeQuery(id+"F3.opRevolve","SWEPT_EDGE",EDGE,{"disambiguationData":[OSD([subQ0,subQ4])]})})})})})})})})});}
            fillet(context, id + "F6", {"entities" : qUnion([Q0, Q1, Q2, Q3, Q4, Q5, Q6, Q7, Q8, Q9]), "radius" : 5 * mm, "tangentPropagation" : true, "allowEdgeOverflow" : false});
        }
        {
            var Q0;
            Q0=makeQuery(id+"F0.imprint","IMPRINT",FACE,{"disambiguationData":[TD([[makeQuery(id+"F0.imprint","IMPRINT",EDGE,{"derivedFrom":sQuery(id+"F0.wireOp",EDGE,"E21.0")}),1.0]])]});
            var Q1;
            {var subQ0=sQuery(id+"F0.wireOp",EDGE,"bqb2CW3f-qtDE-810B-vVhX-ZT2S4oLEjpGb");Q1=makeQuery(id+"F0.imprint","IMPRINT",FACE,{"disambiguationData":[TD([[makeQuery(id+"F0.imprint","IMPRINT",EDGE,{"derivedFrom":subQ0}),1.0]])]});}
            var Q2;
            Q2=sQuery(id+"F0.wireOp",EDGE,"E28");
            revolve(context, id + "F7", {"entities" : qUnion([Q0, Q1]), "axis" : qUnion([Q2]), "revolveType" : RevolveType.FULL});
        }
    });
